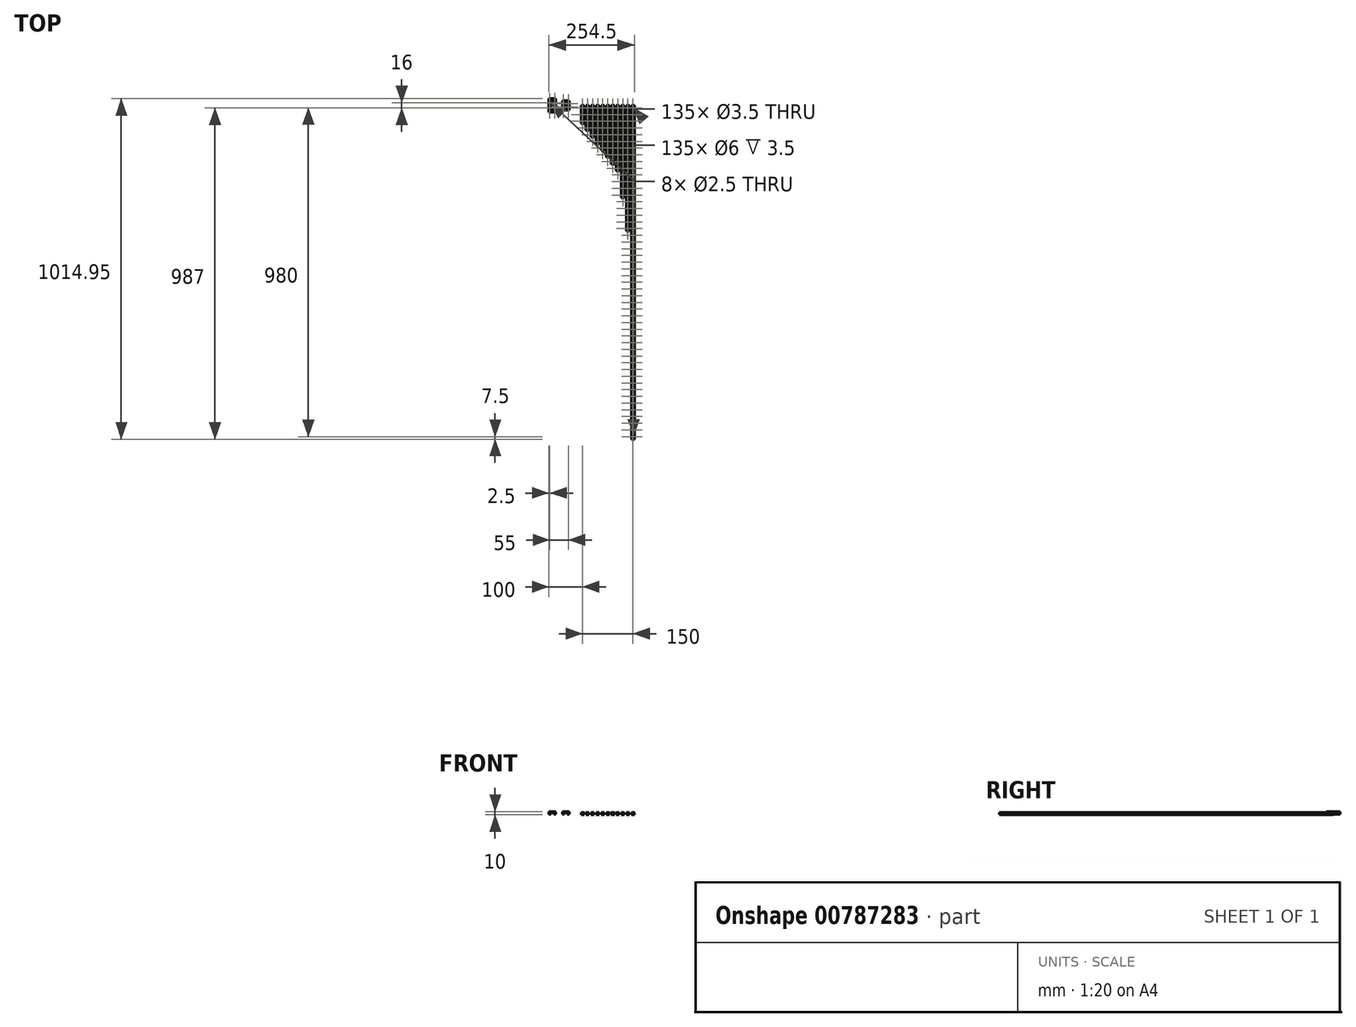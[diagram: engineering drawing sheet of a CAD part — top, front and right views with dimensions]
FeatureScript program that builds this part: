
annotation { "Feature Type Name" : "Feature", "Feature Type Description" : "" }
export const myFeature = defineFeature(function(context is Context, id is Id, definition is map)
    precondition{}
    {
        {
            var Q0;
            Q0=qCreatedBy(makeId("Front.planeOp"),FACE);
            var sketch = newSketch(context, id + "F0", { "sketchPlane" : qUnion([Q0])});
            skPoint(sketch, "E0.middle", {"position": v(0, 0) * mm});
            skLineSegment(sketch, "E1.bottom", {"start": v(4.15, -3.25) * mm, "end": v(-4.15, -3.25) * mm});
            skLineSegment(sketch, "E1.top", {"start": v(4.15, 3.25) * mm, "end": v(-4.15, 3.25) * mm});
            skLineSegment(sketch, "E1.left", {"start": v(4.5, -2.9) * mm, "end": v(4.5, 0.28) * mm});
            skLineSegment(sketch, "E1.right", {"start": v(-4.5, -2.9) * mm, "end": v(-4.5, 0.28) * mm});
            skArc(sketch, "E2", {"start": v(-4.5, 0.28) * mm, "mid": v(-4.1, 0.49) * mm, "end": v(-3.83, 0.85) * mm});
            skArc(sketch, "E3", {"start": v(4.5, 2.22) * mm, "mid": v(4.1, 2.01) * mm, "end": v(3.83, 1.65) * mm});
            skLineSegment(sketch, "E4", {"start": v(3.3, 1.65) * mm, "end": v(3.83, 1.65) * mm});
            skLineSegment(sketch, "E5", {"start": v(3.3, 0.85) * mm, "end": v(3.83, 0.85) * mm});
            skLineSegment(sketch, "E6", {"start": v(-3.3, 0.85) * mm, "end": v(-3.83, 0.85) * mm});
            skLineSegment(sketch, "E7", {"start": v(-3.3, 1.65) * mm, "end": v(-3.83, 1.65) * mm});
            skLineSegment(sketch, "E8", {"start": v(-4.5, 2.9) * mm, "end": v(-4.15, 3.25) * mm});
            skLineSegment(sketch, "E9.MirrorCS", {"start": v(4.5, 2.9) * mm, "end": v(4.15, 3.25) * mm});
            skLineSegment(sketch, "E10.MirrorCS", {"start": v(4.5, -2.9) * mm, "end": v(4.15, -3.25) * mm});
            skLineSegment(sketch, "E11.MirrorCS", {"start": v(-4.5, -2.9) * mm, "end": v(-4.15, -3.25) * mm});
            skPoint(sketch, "E12.orphan", {"position": v(-4.5, 3.25) * mm});
            skLineSegment(sketch, "E13.trimOffspring", {"start": v(-4.5, 2.22) * mm, "end": v(-4.5, 2.9) * mm});
            skArc(sketch, "E14.trimOffspring", {"start": v(-3.83, 1.65) * mm, "mid": v(-4.1, 2.01) * mm, "end": v(-4.5, 2.22) * mm});
            skPoint(sketch, "E15.orphan", {"position": v(4.5, 3.25) * mm});
            skLineSegment(sketch, "E16.trimOffspring", {"start": v(4.5, 2.22) * mm, "end": v(4.5, 2.9) * mm});
            skArc(sketch, "E17.trimOffspring", {"start": v(3.83, 0.85) * mm, "mid": v(4.1, 0.49) * mm, "end": v(4.5, 0.28) * mm});
            skPoint(sketch, "E18.orphan", {"position": v(4.5, -3.25) * mm});
            skPoint(sketch, "E19.orphan", {"position": v(-4.5, -3.25) * mm});
            skLineSegment(sketch, "E20", {"start": v(-3.3, 1.65) * mm, "end": v(-3.3, 0.85) * mm});
            skLineSegment(sketch, "E21", {"start": v(3.3, 1.65) * mm, "end": v(3.3, 0.85) * mm});
            skLineSegment(sketch, "E22", {"start": v(-4.75, 1.25) * mm, "end": v(4.75, 1.25) * mm, "construction": true});
            skLineSegment(sketch, "E23.1.0.0", {"start": v(10.25, 1.25) * mm, "end": v(19.75, 1.25) * mm, "construction": true});
            skLineSegment(sketch, "E23.1.0.1", {"start": v(10.5, -2.9) * mm, "end": v(10.5, 0.28) * mm});
            skLineSegment(sketch, "E23.1.0.2", {"start": v(19.5, -2.9) * mm, "end": v(19.5, 0.28) * mm});
            skLineSegment(sketch, "E23.1.0.3", {"start": v(19.15, -3.25) * mm, "end": v(10.85, -3.25) * mm});
            skLineSegment(sketch, "E23.1.0.4", {"start": v(19.15, 3.25) * mm, "end": v(10.85, 3.25) * mm});
            skPoint(sketch, "E23.1.0.5", {"position": v(15, 0) * mm});
            skPoint(sketch, "E23.1.0.6", {"position": v(10.5, -3.25) * mm});
            skPoint(sketch, "E23.1.0.7", {"position": v(10.5, 3.25) * mm});
            skPoint(sketch, "E23.1.0.8", {"position": v(19.5, 3.25) * mm});
            skPoint(sketch, "E23.1.0.9", {"position": v(19.5, -3.25) * mm});
            skPoint(sketch, "E23.1.0.10", {"position": v(15, 0) * mm});
            skLineSegment(sketch, "E23.1.0.11", {"start": v(19.5, -2.9) * mm, "end": v(19.15, -3.25) * mm});
            skLineSegment(sketch, "E23.1.0.12", {"start": v(19.5, 2.9) * mm, "end": v(19.15, 3.25) * mm});
            skLineSegment(sketch, "E23.1.0.13", {"start": v(10.5, -2.9) * mm, "end": v(10.85, -3.25) * mm});
            skLineSegment(sketch, "E23.1.0.14", {"start": v(11.7, 1.65) * mm, "end": v(11.17, 1.65) * mm});
            skLineSegment(sketch, "E23.1.0.15", {"start": v(10.5, 2.22) * mm, "end": v(10.5, 2.9) * mm});
            skLineSegment(sketch, "E23.1.0.16", {"start": v(19.5, 2.22) * mm, "end": v(19.5, 2.9) * mm});
            skArc(sketch, "E23.1.0.17", {"start": v(18.83, 0.85) * mm, "mid": v(19.1, 0.49) * mm, "end": v(19.5, 0.28) * mm});
            skLineSegment(sketch, "E23.1.0.18", {"start": v(11.7, 1.65) * mm, "end": v(11.7, 0.85) * mm});
            skLineSegment(sketch, "E23.1.0.19", {"start": v(18.3, 0.85) * mm, "end": v(18.83, 0.85) * mm});
            skLineSegment(sketch, "E23.1.0.20", {"start": v(11.7, 0.85) * mm, "end": v(11.17, 0.85) * mm});
            skArc(sketch, "E23.1.0.21", {"start": v(10.5, 0.28) * mm, "mid": v(10.9, 0.49) * mm, "end": v(11.17, 0.85) * mm});
            skLineSegment(sketch, "E23.1.0.22", {"start": v(10.5, 2.9) * mm, "end": v(10.85, 3.25) * mm});
            skArc(sketch, "E23.1.0.23", {"start": v(11.17, 1.65) * mm, "mid": v(10.9, 2.01) * mm, "end": v(10.5, 2.22) * mm});
            skLineSegment(sketch, "E23.1.0.24", {"start": v(18.3, 1.65) * mm, "end": v(18.83, 1.65) * mm});
            skArc(sketch, "E23.1.0.25", {"start": v(19.5, 2.22) * mm, "mid": v(19.1, 2.01) * mm, "end": v(18.83, 1.65) * mm});
            skArc(sketch, "E23.1.0.26", {"start": v(18.83, 0.85) * mm, "mid": v(19.1, 0.49) * mm, "end": v(19.5, 0.28) * mm});
            skLineSegment(sketch, "E23.1.0.27", {"start": v(18.3, 1.65) * mm, "end": v(18.3, 0.85) * mm});
            skLineSegment(sketch, "E23.2.0.0", {"start": v(25.25, 1.25) * mm, "end": v(34.75, 1.25) * mm, "construction": true});
            skLineSegment(sketch, "E23.2.0.1", {"start": v(25.5, -2.9) * mm, "end": v(25.5, 0.28) * mm});
            skLineSegment(sketch, "E23.2.0.2", {"start": v(34.5, -2.9) * mm, "end": v(34.5, 0.28) * mm});
            skLineSegment(sketch, "E23.2.0.3", {"start": v(34.15, -3.25) * mm, "end": v(25.85, -3.25) * mm});
            skLineSegment(sketch, "E23.2.0.4", {"start": v(34.15, 3.25) * mm, "end": v(25.85, 3.25) * mm});
            skPoint(sketch, "E23.2.0.5", {"position": v(30, 0) * mm});
            skPoint(sketch, "E23.2.0.6", {"position": v(25.5, -3.25) * mm});
            skPoint(sketch, "E23.2.0.7", {"position": v(25.5, 3.25) * mm});
            skPoint(sketch, "E23.2.0.8", {"position": v(34.5, 3.25) * mm});
            skPoint(sketch, "E23.2.0.9", {"position": v(34.5, -3.25) * mm});
            skPoint(sketch, "E23.2.0.10", {"position": v(30, 0) * mm});
            skLineSegment(sketch, "E23.2.0.11", {"start": v(34.5, -2.9) * mm, "end": v(34.15, -3.25) * mm});
            skLineSegment(sketch, "E23.2.0.12", {"start": v(34.5, 2.9) * mm, "end": v(34.15, 3.25) * mm});
            skLineSegment(sketch, "E23.2.0.13", {"start": v(25.5, -2.9) * mm, "end": v(25.85, -3.25) * mm});
            skLineSegment(sketch, "E23.2.0.14", {"start": v(26.7, 1.65) * mm, "end": v(26.17, 1.65) * mm});
            skLineSegment(sketch, "E23.2.0.15", {"start": v(25.5, 2.22) * mm, "end": v(25.5, 2.9) * mm});
            skLineSegment(sketch, "E23.2.0.16", {"start": v(34.5, 2.22) * mm, "end": v(34.5, 2.9) * mm});
            skArc(sketch, "E23.2.0.17", {"start": v(33.83, 0.85) * mm, "mid": v(34.1, 0.49) * mm, "end": v(34.5, 0.28) * mm});
            skLineSegment(sketch, "E23.2.0.18", {"start": v(26.7, 1.65) * mm, "end": v(26.7, 0.85) * mm});
            skLineSegment(sketch, "E23.2.0.19", {"start": v(33.3, 0.85) * mm, "end": v(33.83, 0.85) * mm});
            skLineSegment(sketch, "E23.2.0.20", {"start": v(26.7, 0.85) * mm, "end": v(26.17, 0.85) * mm});
            skArc(sketch, "E23.2.0.21", {"start": v(25.5, 0.28) * mm, "mid": v(25.9, 0.49) * mm, "end": v(26.17, 0.85) * mm});
            skLineSegment(sketch, "E23.2.0.22", {"start": v(25.5, 2.9) * mm, "end": v(25.85, 3.25) * mm});
            skArc(sketch, "E23.2.0.23", {"start": v(26.17, 1.65) * mm, "mid": v(25.9, 2.01) * mm, "end": v(25.5, 2.22) * mm});
            skLineSegment(sketch, "E23.2.0.24", {"start": v(33.3, 1.65) * mm, "end": v(33.83, 1.65) * mm});
            skArc(sketch, "E23.2.0.25", {"start": v(34.5, 2.22) * mm, "mid": v(34.1, 2.01) * mm, "end": v(33.83, 1.65) * mm});
            skArc(sketch, "E23.2.0.26", {"start": v(33.83, 0.85) * mm, "mid": v(34.1, 0.49) * mm, "end": v(34.5, 0.28) * mm});
            skLineSegment(sketch, "E23.2.0.27", {"start": v(33.3, 1.65) * mm, "end": v(33.3, 0.85) * mm});
            skLineSegment(sketch, "E23.3.0.0", {"start": v(40.25, 1.25) * mm, "end": v(49.75, 1.25) * mm, "construction": true});
            skLineSegment(sketch, "E23.3.0.1", {"start": v(40.5, -2.9) * mm, "end": v(40.5, 0.28) * mm});
            skLineSegment(sketch, "E23.3.0.2", {"start": v(49.5, -2.9) * mm, "end": v(49.5, 0.28) * mm});
            skLineSegment(sketch, "E23.3.0.3", {"start": v(49.15, -3.25) * mm, "end": v(40.85, -3.25) * mm});
            skLineSegment(sketch, "E23.3.0.4", {"start": v(49.15, 3.25) * mm, "end": v(40.85, 3.25) * mm});
            skPoint(sketch, "E23.3.0.5", {"position": v(45, 0) * mm});
            skPoint(sketch, "E23.3.0.6", {"position": v(40.5, -3.25) * mm});
            skPoint(sketch, "E23.3.0.7", {"position": v(40.5, 3.25) * mm});
            skPoint(sketch, "E23.3.0.8", {"position": v(49.5, 3.25) * mm});
            skPoint(sketch, "E23.3.0.9", {"position": v(49.5, -3.25) * mm});
            skPoint(sketch, "E23.3.0.10", {"position": v(45, 0) * mm});
            skLineSegment(sketch, "E23.3.0.11", {"start": v(49.5, -2.9) * mm, "end": v(49.15, -3.25) * mm});
            skLineSegment(sketch, "E23.3.0.12", {"start": v(49.5, 2.9) * mm, "end": v(49.15, 3.25) * mm});
            skLineSegment(sketch, "E23.3.0.13", {"start": v(40.5, -2.9) * mm, "end": v(40.85, -3.25) * mm});
            skLineSegment(sketch, "E23.3.0.14", {"start": v(41.7, 1.65) * mm, "end": v(41.17, 1.65) * mm});
            skLineSegment(sketch, "E23.3.0.15", {"start": v(40.5, 2.22) * mm, "end": v(40.5, 2.9) * mm});
            skLineSegment(sketch, "E23.3.0.16", {"start": v(49.5, 2.22) * mm, "end": v(49.5, 2.9) * mm});
            skArc(sketch, "E23.3.0.17", {"start": v(48.83, 0.85) * mm, "mid": v(49.1, 0.49) * mm, "end": v(49.5, 0.28) * mm});
            skLineSegment(sketch, "E23.3.0.18", {"start": v(41.7, 1.65) * mm, "end": v(41.7, 0.85) * mm});
            skLineSegment(sketch, "E23.3.0.19", {"start": v(48.3, 0.85) * mm, "end": v(48.83, 0.85) * mm});
            skLineSegment(sketch, "E23.3.0.20", {"start": v(41.7, 0.85) * mm, "end": v(41.17, 0.85) * mm});
            skArc(sketch, "E23.3.0.21", {"start": v(40.5, 0.28) * mm, "mid": v(40.9, 0.49) * mm, "end": v(41.17, 0.85) * mm});
            skLineSegment(sketch, "E23.3.0.22", {"start": v(40.5, 2.9) * mm, "end": v(40.85, 3.25) * mm});
            skArc(sketch, "E23.3.0.23", {"start": v(41.17, 1.65) * mm, "mid": v(40.9, 2.01) * mm, "end": v(40.5, 2.22) * mm});
            skLineSegment(sketch, "E23.3.0.24", {"start": v(48.3, 1.65) * mm, "end": v(48.83, 1.65) * mm});
            skArc(sketch, "E23.3.0.25", {"start": v(49.5, 2.22) * mm, "mid": v(49.1, 2.01) * mm, "end": v(48.83, 1.65) * mm});
            skArc(sketch, "E23.3.0.26", {"start": v(48.83, 0.85) * mm, "mid": v(49.1, 0.49) * mm, "end": v(49.5, 0.28) * mm});
            skLineSegment(sketch, "E23.3.0.27", {"start": v(48.3, 1.65) * mm, "end": v(48.3, 0.85) * mm});
            skLineSegment(sketch, "E23.4.0.0", {"start": v(55.25, 1.25) * mm, "end": v(64.75, 1.25) * mm, "construction": true});
            skLineSegment(sketch, "E23.4.0.1", {"start": v(55.5, -2.9) * mm, "end": v(55.5, 0.28) * mm});
            skLineSegment(sketch, "E23.4.0.2", {"start": v(64.5, -2.9) * mm, "end": v(64.5, 0.28) * mm});
            skLineSegment(sketch, "E23.4.0.3", {"start": v(64.15, -3.25) * mm, "end": v(55.85, -3.25) * mm});
            skLineSegment(sketch, "E23.4.0.4", {"start": v(64.15, 3.25) * mm, "end": v(55.85, 3.25) * mm});
            skPoint(sketch, "E23.4.0.5", {"position": v(60, 0) * mm});
            skPoint(sketch, "E23.4.0.6", {"position": v(55.5, -3.25) * mm});
            skPoint(sketch, "E23.4.0.7", {"position": v(55.5, 3.25) * mm});
            skPoint(sketch, "E23.4.0.8", {"position": v(64.5, 3.25) * mm});
            skPoint(sketch, "E23.4.0.9", {"position": v(64.5, -3.25) * mm});
            skPoint(sketch, "E23.4.0.10", {"position": v(60, 0) * mm});
            skLineSegment(sketch, "E23.4.0.11", {"start": v(64.5, -2.9) * mm, "end": v(64.15, -3.25) * mm});
            skLineSegment(sketch, "E23.4.0.12", {"start": v(64.5, 2.9) * mm, "end": v(64.15, 3.25) * mm});
            skLineSegment(sketch, "E23.4.0.13", {"start": v(55.5, -2.9) * mm, "end": v(55.85, -3.25) * mm});
            skLineSegment(sketch, "E23.4.0.14", {"start": v(56.7, 1.65) * mm, "end": v(56.17, 1.65) * mm});
            skLineSegment(sketch, "E23.4.0.15", {"start": v(55.5, 2.22) * mm, "end": v(55.5, 2.9) * mm});
            skLineSegment(sketch, "E23.4.0.16", {"start": v(64.5, 2.22) * mm, "end": v(64.5, 2.9) * mm});
            skArc(sketch, "E23.4.0.17", {"start": v(63.83, 0.85) * mm, "mid": v(64.1, 0.49) * mm, "end": v(64.5, 0.28) * mm});
            skLineSegment(sketch, "E23.4.0.18", {"start": v(56.7, 1.65) * mm, "end": v(56.7, 0.85) * mm});
            skLineSegment(sketch, "E23.4.0.19", {"start": v(63.3, 0.85) * mm, "end": v(63.83, 0.85) * mm});
            skLineSegment(sketch, "E23.4.0.20", {"start": v(56.7, 0.85) * mm, "end": v(56.17, 0.85) * mm});
            skArc(sketch, "E23.4.0.21", {"start": v(55.5, 0.28) * mm, "mid": v(55.9, 0.49) * mm, "end": v(56.17, 0.85) * mm});
            skLineSegment(sketch, "E23.4.0.22", {"start": v(55.5, 2.9) * mm, "end": v(55.85, 3.25) * mm});
            skArc(sketch, "E23.4.0.23", {"start": v(56.17, 1.65) * mm, "mid": v(55.9, 2.01) * mm, "end": v(55.5, 2.22) * mm});
            skLineSegment(sketch, "E23.4.0.24", {"start": v(63.3, 1.65) * mm, "end": v(63.83, 1.65) * mm});
            skArc(sketch, "E23.4.0.25", {"start": v(64.5, 2.22) * mm, "mid": v(64.1, 2.01) * mm, "end": v(63.83, 1.65) * mm});
            skArc(sketch, "E23.4.0.26", {"start": v(63.83, 0.85) * mm, "mid": v(64.1, 0.49) * mm, "end": v(64.5, 0.28) * mm});
            skLineSegment(sketch, "E23.4.0.27", {"start": v(63.3, 1.65) * mm, "end": v(63.3, 0.85) * mm});
            skLineSegment(sketch, "E23.5.0.0", {"start": v(70.25, 1.25) * mm, "end": v(79.75, 1.25) * mm, "construction": true});
            skLineSegment(sketch, "E23.5.0.1", {"start": v(70.5, -2.9) * mm, "end": v(70.5, 0.28) * mm});
            skLineSegment(sketch, "E23.5.0.2", {"start": v(79.5, -2.9) * mm, "end": v(79.5, 0.28) * mm});
            skLineSegment(sketch, "E23.5.0.3", {"start": v(79.15, -3.25) * mm, "end": v(70.85, -3.25) * mm});
            skLineSegment(sketch, "E23.5.0.4", {"start": v(79.15, 3.25) * mm, "end": v(70.85, 3.25) * mm});
            skPoint(sketch, "E23.5.0.5", {"position": v(75, 0) * mm});
            skPoint(sketch, "E23.5.0.6", {"position": v(70.5, -3.25) * mm});
            skPoint(sketch, "E23.5.0.7", {"position": v(70.5, 3.25) * mm});
            skPoint(sketch, "E23.5.0.8", {"position": v(79.5, 3.25) * mm});
            skPoint(sketch, "E23.5.0.9", {"position": v(79.5, -3.25) * mm});
            skPoint(sketch, "E23.5.0.10", {"position": v(75, 0) * mm});
            skLineSegment(sketch, "E23.5.0.11", {"start": v(79.5, -2.9) * mm, "end": v(79.15, -3.25) * mm});
            skLineSegment(sketch, "E23.5.0.12", {"start": v(79.5, 2.9) * mm, "end": v(79.15, 3.25) * mm});
            skLineSegment(sketch, "E23.5.0.13", {"start": v(70.5, -2.9) * mm, "end": v(70.85, -3.25) * mm});
            skLineSegment(sketch, "E23.5.0.14", {"start": v(71.7, 1.65) * mm, "end": v(71.17, 1.65) * mm});
            skLineSegment(sketch, "E23.5.0.15", {"start": v(70.5, 2.22) * mm, "end": v(70.5, 2.9) * mm});
            skLineSegment(sketch, "E23.5.0.16", {"start": v(79.5, 2.22) * mm, "end": v(79.5, 2.9) * mm});
            skArc(sketch, "E23.5.0.17", {"start": v(78.83, 0.85) * mm, "mid": v(79.1, 0.49) * mm, "end": v(79.5, 0.28) * mm});
            skLineSegment(sketch, "E23.5.0.18", {"start": v(71.7, 1.65) * mm, "end": v(71.7, 0.85) * mm});
            skLineSegment(sketch, "E23.5.0.19", {"start": v(78.3, 0.85) * mm, "end": v(78.83, 0.85) * mm});
            skLineSegment(sketch, "E23.5.0.20", {"start": v(71.7, 0.85) * mm, "end": v(71.17, 0.85) * mm});
            skArc(sketch, "E23.5.0.21", {"start": v(70.5, 0.28) * mm, "mid": v(70.9, 0.49) * mm, "end": v(71.17, 0.85) * mm});
            skLineSegment(sketch, "E23.5.0.22", {"start": v(70.5, 2.9) * mm, "end": v(70.85, 3.25) * mm});
            skArc(sketch, "E23.5.0.23", {"start": v(71.17, 1.65) * mm, "mid": v(70.9, 2.01) * mm, "end": v(70.5, 2.22) * mm});
            skLineSegment(sketch, "E23.5.0.24", {"start": v(78.3, 1.65) * mm, "end": v(78.83, 1.65) * mm});
            skArc(sketch, "E23.5.0.25", {"start": v(79.5, 2.22) * mm, "mid": v(79.1, 2.01) * mm, "end": v(78.83, 1.65) * mm});
            skArc(sketch, "E23.5.0.26", {"start": v(78.83, 0.85) * mm, "mid": v(79.1, 0.49) * mm, "end": v(79.5, 0.28) * mm});
            skLineSegment(sketch, "E23.5.0.27", {"start": v(78.3, 1.65) * mm, "end": v(78.3, 0.85) * mm});
            skLineSegment(sketch, "E23.6.0.0", {"start": v(85.25, 1.25) * mm, "end": v(94.75, 1.25) * mm, "construction": true});
            skLineSegment(sketch, "E23.6.0.1", {"start": v(85.5, -2.9) * mm, "end": v(85.5, 0.28) * mm});
            skLineSegment(sketch, "E23.6.0.2", {"start": v(94.5, -2.9) * mm, "end": v(94.5, 0.28) * mm});
            skLineSegment(sketch, "E23.6.0.3", {"start": v(94.15, -3.25) * mm, "end": v(85.85, -3.25) * mm});
            skLineSegment(sketch, "E23.6.0.4", {"start": v(94.15, 3.25) * mm, "end": v(85.85, 3.25) * mm});
            skPoint(sketch, "E23.6.0.5", {"position": v(90, 0) * mm});
            skPoint(sketch, "E23.6.0.6", {"position": v(85.5, -3.25) * mm});
            skPoint(sketch, "E23.6.0.7", {"position": v(85.5, 3.25) * mm});
            skPoint(sketch, "E23.6.0.8", {"position": v(94.5, 3.25) * mm});
            skPoint(sketch, "E23.6.0.9", {"position": v(94.5, -3.25) * mm});
            skPoint(sketch, "E23.6.0.10", {"position": v(90, 0) * mm});
            skLineSegment(sketch, "E23.6.0.11", {"start": v(94.5, -2.9) * mm, "end": v(94.15, -3.25) * mm});
            skLineSegment(sketch, "E23.6.0.12", {"start": v(94.5, 2.9) * mm, "end": v(94.15, 3.25) * mm});
            skLineSegment(sketch, "E23.6.0.13", {"start": v(85.5, -2.9) * mm, "end": v(85.85, -3.25) * mm});
            skLineSegment(sketch, "E23.6.0.14", {"start": v(86.7, 1.65) * mm, "end": v(86.17, 1.65) * mm});
            skLineSegment(sketch, "E23.6.0.15", {"start": v(85.5, 2.22) * mm, "end": v(85.5, 2.9) * mm});
            skLineSegment(sketch, "E23.6.0.16", {"start": v(94.5, 2.22) * mm, "end": v(94.5, 2.9) * mm});
            skArc(sketch, "E23.6.0.17", {"start": v(93.83, 0.85) * mm, "mid": v(94.1, 0.49) * mm, "end": v(94.5, 0.28) * mm});
            skLineSegment(sketch, "E23.6.0.18", {"start": v(86.7, 1.65) * mm, "end": v(86.7, 0.85) * mm});
            skLineSegment(sketch, "E23.6.0.19", {"start": v(93.3, 0.85) * mm, "end": v(93.83, 0.85) * mm});
            skLineSegment(sketch, "E23.6.0.20", {"start": v(86.7, 0.85) * mm, "end": v(86.17, 0.85) * mm});
            skArc(sketch, "E23.6.0.21", {"start": v(85.5, 0.28) * mm, "mid": v(85.9, 0.49) * mm, "end": v(86.17, 0.85) * mm});
            skLineSegment(sketch, "E23.6.0.22", {"start": v(85.5, 2.9) * mm, "end": v(85.85, 3.25) * mm});
            skArc(sketch, "E23.6.0.23", {"start": v(86.17, 1.65) * mm, "mid": v(85.9, 2.01) * mm, "end": v(85.5, 2.22) * mm});
            skLineSegment(sketch, "E23.6.0.24", {"start": v(93.3, 1.65) * mm, "end": v(93.83, 1.65) * mm});
            skArc(sketch, "E23.6.0.25", {"start": v(94.5, 2.22) * mm, "mid": v(94.1, 2.01) * mm, "end": v(93.83, 1.65) * mm});
            skArc(sketch, "E23.6.0.26", {"start": v(93.83, 0.85) * mm, "mid": v(94.1, 0.49) * mm, "end": v(94.5, 0.28) * mm});
            skLineSegment(sketch, "E23.6.0.27", {"start": v(93.3, 1.65) * mm, "end": v(93.3, 0.85) * mm});
            skLineSegment(sketch, "E23.direction1", {"start": v(-4.5, -3.25) * mm, "end": v(10.5, -3.25) * mm, "construction": true});
            skLineSegment(sketch, "E24.0.7.0", {"start": v(100.25, 1.25) * mm, "end": v(109.75, 1.25) * mm, "construction": true});
            skLineSegment(sketch, "E24.3.7.0", {"start": v(100.5, -2.9) * mm, "end": v(100.5, 0.28) * mm});
            skLineSegment(sketch, "E24.6.7.0", {"start": v(109.5, -2.9) * mm, "end": v(109.5, 0.28) * mm});
            skLineSegment(sketch, "E24.9.7.0", {"start": v(109.15, -3.25) * mm, "end": v(100.85, -3.25) * mm});
            skLineSegment(sketch, "E24.12.7.0", {"start": v(109.15, 3.25) * mm, "end": v(100.85, 3.25) * mm});
            skPoint(sketch, "E24.15.7.0", {"position": v(105, 0) * mm});
            skPoint(sketch, "E24.16.7.0", {"position": v(100.5, -3.25) * mm});
            skPoint(sketch, "E24.17.7.0", {"position": v(100.5, 3.25) * mm});
            skPoint(sketch, "E24.18.7.0", {"position": v(109.5, 3.25) * mm});
            skPoint(sketch, "E24.19.7.0", {"position": v(109.5, -3.25) * mm});
            skPoint(sketch, "E24.20.7.0", {"position": v(105, 0) * mm});
            skLineSegment(sketch, "E24.21.7.0", {"start": v(109.5, -2.9) * mm, "end": v(109.15, -3.25) * mm});
            skLineSegment(sketch, "E24.24.7.0", {"start": v(109.5, 2.9) * mm, "end": v(109.15, 3.25) * mm});
            skLineSegment(sketch, "E24.27.7.0", {"start": v(100.5, -2.9) * mm, "end": v(100.85, -3.25) * mm});
            skLineSegment(sketch, "E24.30.7.0", {"start": v(101.7, 1.65) * mm, "end": v(101.17, 1.65) * mm});
            skLineSegment(sketch, "E24.33.7.0", {"start": v(100.5, 2.22) * mm, "end": v(100.5, 2.9) * mm});
            skLineSegment(sketch, "E24.36.7.0", {"start": v(109.5, 2.22) * mm, "end": v(109.5, 2.9) * mm});
            skArc(sketch, "E24.39.7.0", {"start": v(108.83, 0.85) * mm, "mid": v(109.1, 0.49) * mm, "end": v(109.5, 0.28) * mm});
            skLineSegment(sketch, "E24.43.7.0", {"start": v(101.7, 1.65) * mm, "end": v(101.7, 0.85) * mm});
            skLineSegment(sketch, "E24.46.7.0", {"start": v(108.3, 0.85) * mm, "end": v(108.83, 0.85) * mm});
            skLineSegment(sketch, "E24.49.7.0", {"start": v(101.7, 0.85) * mm, "end": v(101.17, 0.85) * mm});
            skArc(sketch, "E24.52.7.0", {"start": v(100.5, 0.28) * mm, "mid": v(100.9, 0.49) * mm, "end": v(101.17, 0.85) * mm});
            skLineSegment(sketch, "E24.56.7.0", {"start": v(100.5, 2.9) * mm, "end": v(100.85, 3.25) * mm});
            skArc(sketch, "E24.59.7.0", {"start": v(101.17, 1.65) * mm, "mid": v(100.9, 2.01) * mm, "end": v(100.5, 2.22) * mm});
            skLineSegment(sketch, "E24.63.7.0", {"start": v(108.3, 1.65) * mm, "end": v(108.83, 1.65) * mm});
            skArc(sketch, "E24.66.7.0", {"start": v(109.5, 2.22) * mm, "mid": v(109.1, 2.01) * mm, "end": v(108.83, 1.65) * mm});
            skArc(sketch, "E24.70.7.0", {"start": v(108.83, 0.85) * mm, "mid": v(109.1, 0.49) * mm, "end": v(109.5, 0.28) * mm});
            skLineSegment(sketch, "E24.74.7.0", {"start": v(108.3, 1.65) * mm, "end": v(108.3, 0.85) * mm});
            skLineSegment(sketch, "E24.0.8.0", {"start": v(115.25, 1.25) * mm, "end": v(124.75, 1.25) * mm, "construction": true});
            skLineSegment(sketch, "E24.3.8.0", {"start": v(115.5, -2.9) * mm, "end": v(115.5, 0.28) * mm});
            skLineSegment(sketch, "E24.6.8.0", {"start": v(124.5, -2.9) * mm, "end": v(124.5, 0.28) * mm});
            skLineSegment(sketch, "E24.9.8.0", {"start": v(124.15, -3.25) * mm, "end": v(115.85, -3.25) * mm});
            skLineSegment(sketch, "E24.12.8.0", {"start": v(124.15, 3.25) * mm, "end": v(115.85, 3.25) * mm});
            skPoint(sketch, "E24.15.8.0", {"position": v(120, 0) * mm});
            skPoint(sketch, "E24.16.8.0", {"position": v(115.5, -3.25) * mm});
            skPoint(sketch, "E24.17.8.0", {"position": v(115.5, 3.25) * mm});
            skPoint(sketch, "E24.18.8.0", {"position": v(124.5, 3.25) * mm});
            skPoint(sketch, "E24.19.8.0", {"position": v(124.5, -3.25) * mm});
            skPoint(sketch, "E24.20.8.0", {"position": v(120, 0) * mm});
            skLineSegment(sketch, "E24.21.8.0", {"start": v(124.5, -2.9) * mm, "end": v(124.15, -3.25) * mm});
            skLineSegment(sketch, "E24.24.8.0", {"start": v(124.5, 2.9) * mm, "end": v(124.15, 3.25) * mm});
            skLineSegment(sketch, "E24.27.8.0", {"start": v(115.5, -2.9) * mm, "end": v(115.85, -3.25) * mm});
            skLineSegment(sketch, "E24.30.8.0", {"start": v(116.7, 1.65) * mm, "end": v(116.17, 1.65) * mm});
            skLineSegment(sketch, "E24.33.8.0", {"start": v(115.5, 2.22) * mm, "end": v(115.5, 2.9) * mm});
            skLineSegment(sketch, "E24.36.8.0", {"start": v(124.5, 2.22) * mm, "end": v(124.5, 2.9) * mm});
            skArc(sketch, "E24.39.8.0", {"start": v(123.83, 0.85) * mm, "mid": v(124.1, 0.49) * mm, "end": v(124.5, 0.28) * mm});
            skLineSegment(sketch, "E24.43.8.0", {"start": v(116.7, 1.65) * mm, "end": v(116.7, 0.85) * mm});
            skLineSegment(sketch, "E24.46.8.0", {"start": v(123.3, 0.85) * mm, "end": v(123.83, 0.85) * mm});
            skLineSegment(sketch, "E24.49.8.0", {"start": v(116.7, 0.85) * mm, "end": v(116.17, 0.85) * mm});
            skArc(sketch, "E24.52.8.0", {"start": v(115.5, 0.28) * mm, "mid": v(115.9, 0.49) * mm, "end": v(116.17, 0.85) * mm});
            skLineSegment(sketch, "E24.56.8.0", {"start": v(115.5, 2.9) * mm, "end": v(115.85, 3.25) * mm});
            skArc(sketch, "E24.59.8.0", {"start": v(116.17, 1.65) * mm, "mid": v(115.9, 2.01) * mm, "end": v(115.5, 2.22) * mm});
            skLineSegment(sketch, "E24.63.8.0", {"start": v(123.3, 1.65) * mm, "end": v(123.83, 1.65) * mm});
            skArc(sketch, "E24.66.8.0", {"start": v(124.5, 2.22) * mm, "mid": v(124.1, 2.01) * mm, "end": v(123.83, 1.65) * mm});
            skArc(sketch, "E24.70.8.0", {"start": v(123.83, 0.85) * mm, "mid": v(124.1, 0.49) * mm, "end": v(124.5, 0.28) * mm});
            skLineSegment(sketch, "E24.74.8.0", {"start": v(123.3, 1.65) * mm, "end": v(123.3, 0.85) * mm});
            skLineSegment(sketch, "E24.0.9.0", {"start": v(130.25, 1.25) * mm, "end": v(139.75, 1.25) * mm, "construction": true});
            skLineSegment(sketch, "E24.3.9.0", {"start": v(130.5, -2.9) * mm, "end": v(130.5, 0.28) * mm});
            skLineSegment(sketch, "E24.6.9.0", {"start": v(139.5, -2.9) * mm, "end": v(139.5, 0.28) * mm});
            skLineSegment(sketch, "E24.9.9.0", {"start": v(139.15, -3.25) * mm, "end": v(130.85, -3.25) * mm});
            skLineSegment(sketch, "E24.12.9.0", {"start": v(139.15, 3.25) * mm, "end": v(130.85, 3.25) * mm});
            skPoint(sketch, "E24.15.9.0", {"position": v(135, 0) * mm});
            skPoint(sketch, "E24.16.9.0", {"position": v(130.5, -3.25) * mm});
            skPoint(sketch, "E24.17.9.0", {"position": v(130.5, 3.25) * mm});
            skPoint(sketch, "E24.18.9.0", {"position": v(139.5, 3.25) * mm});
            skPoint(sketch, "E24.19.9.0", {"position": v(139.5, -3.25) * mm});
            skPoint(sketch, "E24.20.9.0", {"position": v(135, 0) * mm});
            skLineSegment(sketch, "E24.21.9.0", {"start": v(139.5, -2.9) * mm, "end": v(139.15, -3.25) * mm});
            skLineSegment(sketch, "E24.24.9.0", {"start": v(139.5, 2.9) * mm, "end": v(139.15, 3.25) * mm});
            skLineSegment(sketch, "E24.27.9.0", {"start": v(130.5, -2.9) * mm, "end": v(130.85, -3.25) * mm});
            skLineSegment(sketch, "E24.30.9.0", {"start": v(131.7, 1.65) * mm, "end": v(131.17, 1.65) * mm});
            skLineSegment(sketch, "E24.33.9.0", {"start": v(130.5, 2.22) * mm, "end": v(130.5, 2.9) * mm});
            skLineSegment(sketch, "E24.36.9.0", {"start": v(139.5, 2.22) * mm, "end": v(139.5, 2.9) * mm});
            skArc(sketch, "E24.39.9.0", {"start": v(138.83, 0.85) * mm, "mid": v(139.1, 0.49) * mm, "end": v(139.5, 0.28) * mm});
            skLineSegment(sketch, "E24.43.9.0", {"start": v(131.7, 1.65) * mm, "end": v(131.7, 0.85) * mm});
            skLineSegment(sketch, "E24.46.9.0", {"start": v(138.3, 0.85) * mm, "end": v(138.83, 0.85) * mm});
            skLineSegment(sketch, "E24.49.9.0", {"start": v(131.7, 0.85) * mm, "end": v(131.17, 0.85) * mm});
            skArc(sketch, "E24.52.9.0", {"start": v(130.5, 0.28) * mm, "mid": v(130.9, 0.49) * mm, "end": v(131.17, 0.85) * mm});
            skLineSegment(sketch, "E24.56.9.0", {"start": v(130.5, 2.9) * mm, "end": v(130.85, 3.25) * mm});
            skArc(sketch, "E24.59.9.0", {"start": v(131.17, 1.65) * mm, "mid": v(130.9, 2.01) * mm, "end": v(130.5, 2.22) * mm});
            skLineSegment(sketch, "E24.63.9.0", {"start": v(138.3, 1.65) * mm, "end": v(138.83, 1.65) * mm});
            skArc(sketch, "E24.66.9.0", {"start": v(139.5, 2.22) * mm, "mid": v(139.1, 2.01) * mm, "end": v(138.83, 1.65) * mm});
            skArc(sketch, "E24.70.9.0", {"start": v(138.83, 0.85) * mm, "mid": v(139.1, 0.49) * mm, "end": v(139.5, 0.28) * mm});
            skLineSegment(sketch, "E24.74.9.0", {"start": v(138.3, 1.65) * mm, "end": v(138.3, 0.85) * mm});
            skLineSegment(sketch, "E24.0.10.0", {"start": v(145.25, 1.25) * mm, "end": v(154.75, 1.25) * mm, "construction": true});
            skLineSegment(sketch, "E24.3.10.0", {"start": v(145.5, -2.9) * mm, "end": v(145.5, 0.28) * mm});
            skLineSegment(sketch, "E24.6.10.0", {"start": v(154.5, -2.9) * mm, "end": v(154.5, 0.28) * mm});
            skLineSegment(sketch, "E24.9.10.0", {"start": v(154.15, -3.25) * mm, "end": v(145.85, -3.25) * mm});
            skLineSegment(sketch, "E24.12.10.0", {"start": v(154.15, 3.25) * mm, "end": v(145.85, 3.25) * mm});
            skPoint(sketch, "E24.15.10.0", {"position": v(150, 0) * mm});
            skPoint(sketch, "E24.16.10.0", {"position": v(145.5, -3.25) * mm});
            skPoint(sketch, "E24.17.10.0", {"position": v(145.5, 3.25) * mm});
            skPoint(sketch, "E24.18.10.0", {"position": v(154.5, 3.25) * mm});
            skPoint(sketch, "E24.19.10.0", {"position": v(154.5, -3.25) * mm});
            skPoint(sketch, "E24.20.10.0", {"position": v(150, 0) * mm});
            skLineSegment(sketch, "E24.21.10.0", {"start": v(154.5, -2.9) * mm, "end": v(154.15, -3.25) * mm});
            skLineSegment(sketch, "E24.24.10.0", {"start": v(154.5, 2.9) * mm, "end": v(154.15, 3.25) * mm});
            skLineSegment(sketch, "E24.27.10.0", {"start": v(145.5, -2.9) * mm, "end": v(145.85, -3.25) * mm});
            skLineSegment(sketch, "E24.30.10.0", {"start": v(146.7, 1.65) * mm, "end": v(146.17, 1.65) * mm});
            skLineSegment(sketch, "E24.33.10.0", {"start": v(145.5, 2.22) * mm, "end": v(145.5, 2.9) * mm});
            skLineSegment(sketch, "E24.36.10.0", {"start": v(154.5, 2.22) * mm, "end": v(154.5, 2.9) * mm});
            skArc(sketch, "E24.39.10.0", {"start": v(153.83, 0.85) * mm, "mid": v(154.1, 0.49) * mm, "end": v(154.5, 0.28) * mm});
            skLineSegment(sketch, "E24.43.10.0", {"start": v(146.7, 1.65) * mm, "end": v(146.7, 0.85) * mm});
            skLineSegment(sketch, "E24.46.10.0", {"start": v(153.3, 0.85) * mm, "end": v(153.83, 0.85) * mm});
            skLineSegment(sketch, "E24.49.10.0", {"start": v(146.7, 0.85) * mm, "end": v(146.17, 0.85) * mm});
            skArc(sketch, "E24.52.10.0", {"start": v(145.5, 0.28) * mm, "mid": v(145.9, 0.49) * mm, "end": v(146.17, 0.85) * mm});
            skLineSegment(sketch, "E24.56.10.0", {"start": v(145.5, 2.9) * mm, "end": v(145.85, 3.25) * mm});
            skArc(sketch, "E24.59.10.0", {"start": v(146.17, 1.65) * mm, "mid": v(145.9, 2.01) * mm, "end": v(145.5, 2.22) * mm});
            skLineSegment(sketch, "E24.63.10.0", {"start": v(153.3, 1.65) * mm, "end": v(153.83, 1.65) * mm});
            skArc(sketch, "E24.66.10.0", {"start": v(154.5, 2.22) * mm, "mid": v(154.1, 2.01) * mm, "end": v(153.83, 1.65) * mm});
            skArc(sketch, "E24.70.10.0", {"start": v(153.83, 0.85) * mm, "mid": v(154.1, 0.49) * mm, "end": v(154.5, 0.28) * mm});
            skLineSegment(sketch, "E24.74.10.0", {"start": v(153.3, 1.65) * mm, "end": v(153.3, 0.85) * mm});
            skSolve(sketch);
        }
        {
            var Q0;
            Q0=makeQuery(id+"F0.imprint","IMPRINT",FACE,{"disambiguationData":[TD([[makeQuery(id+"F0.imprint","IMPRINT",EDGE,{"derivedFrom":sQuery(id+"F0.wireOp",EDGE,"E1.bottom")}),-1.0]])]});
            extrude(context, id + "F1", {"entities" : qUnion([Q0]), "depth" : 55 * mm, "offsetDistance" : 25 * mm});
        }
        {
            var Q0;
            Q0=makeQuery(id+"F0.imprint","IMPRINT",FACE,{"disambiguationData":[TD([[makeQuery(id+"F0.imprint","IMPRINT",EDGE,{"derivedFrom":sQuery(id+"F0.wireOp",EDGE,"E23.1.0.1")}),-1.0]])]});
            extrude(context, id + "F2", {"entities" : qUnion([Q0]), "depth" : 75 * mm, "offsetDistance" : 25 * mm});
        }
        {
            var Q0;
            Q0=makeQuery(id+"F0.imprint","IMPRINT",FACE,{"disambiguationData":[TD([[makeQuery(id+"F0.imprint","IMPRINT",EDGE,{"derivedFrom":sQuery(id+"F0.wireOp",EDGE,"E23.2.0.1")}),-1.0]])]});
            extrude(context, id + "F3", {"entities" : qUnion([Q0]), "depth" : 95 * mm, "offsetDistance" : 25 * mm});
        }
        {
            var Q0;
            Q0=makeQuery(id+"F0.imprint","IMPRINT",FACE,{"disambiguationData":[TD([[makeQuery(id+"F0.imprint","IMPRINT",EDGE,{"derivedFrom":sQuery(id+"F0.wireOp",EDGE,"E23.3.0.1")}),-1.0]])]});
            extrude(context, id + "F4", {"entities" : qUnion([Q0]), "depth" : 115 * mm, "offsetDistance" : 25 * mm});
        }
        {
            var Q0;
            Q0=makeQuery(id+"F0.imprint","IMPRINT",FACE,{"disambiguationData":[TD([[makeQuery(id+"F0.imprint","IMPRINT",EDGE,{"derivedFrom":sQuery(id+"F0.wireOp",EDGE,"E23.4.0.1")}),-1.0]])]});
            extrude(context, id + "F5", {"entities" : qUnion([Q0]), "depth" : 135 * mm, "offsetDistance" : 25 * mm});
        }
        {
            var Q0;
            Q0=makeQuery(id+"F0.imprint","IMPRINT",FACE,{"disambiguationData":[TD([[makeQuery(id+"F0.imprint","IMPRINT",EDGE,{"derivedFrom":sQuery(id+"F0.wireOp",EDGE,"E23.5.0.1")}),-1.0]])]});
            extrude(context, id + "F6", {"entities" : qUnion([Q0]), "depth" : 155 * mm, "offsetDistance" : 25 * mm});
        }
        {
            var Q0;
            Q0=makeQuery(id+"F0.imprint","IMPRINT",FACE,{"disambiguationData":[TD([[makeQuery(id+"F0.imprint","IMPRINT",EDGE,{"derivedFrom":sQuery(id+"F0.wireOp",EDGE,"E23.6.0.1")}),-1.0]])]});
            extrude(context, id + "F7", {"entities" : qUnion([Q0]), "depth" : 175 * mm, "offsetDistance" : 25 * mm});
        }
        {
            var Q0;
            Q0=makeQuery(id+"F0.imprint","IMPRINT",FACE,{"disambiguationData":[TD([[makeQuery(id+"F0.imprint","IMPRINT",EDGE,{"derivedFrom":sQuery(id+"F0.wireOp",EDGE,"E24.3.7.0")}),-1.0]])]});
            extrude(context, id + "F8", {"entities" : qUnion([Q0]), "depth" : 195 * mm, "offsetDistance" : 25 * mm});
        }
        {
            var Q0;
            Q0=makeQuery(id+"F0.imprint","IMPRINT",FACE,{"disambiguationData":[TD([[makeQuery(id+"F0.imprint","IMPRINT",EDGE,{"derivedFrom":sQuery(id+"F0.wireOp",EDGE,"E24.3.8.0")}),-1.0]])]});
            extrude(context, id + "F9", {"entities" : qUnion([Q0]), "depth" : 275 * mm, "offsetDistance" : 25 * mm});
        }
        {
            var Q0;
            Q0=makeQuery(id+"F0.imprint","IMPRINT",FACE,{"disambiguationData":[TD([[makeQuery(id+"F0.imprint","IMPRINT",EDGE,{"derivedFrom":sQuery(id+"F0.wireOp",EDGE,"E24.3.9.0")}),-1.0]])]});
            extrude(context, id + "F10", {"entities" : qUnion([Q0]), "depth" : 375 * mm, "offsetDistance" : 25 * mm});
        }
        {
            var Q0;
            Q0=makeQuery(id+"F0.imprint","IMPRINT",FACE,{"disambiguationData":[TD([[makeQuery(id+"F0.imprint","IMPRINT",EDGE,{"derivedFrom":sQuery(id+"F0.wireOp",EDGE,"E24.3.10.0")}),-1.0]])]});
            extrude(context, id + "F11", {"entities" : qUnion([Q0]), "depth" : 995 * mm, "offsetDistance" : 25 * mm});
        }
        {
            var Q0;
            Q0=makeQuery(id+"F1.opExtrude","SWEPT_FACE",FACE,{"disambiguationData":[OSD([sQuery(id+"F0.wireOp",EDGE,"E1.top")])]});
            var sketch = newSketch(context, id + "F12", { "sketchPlane" : qUnion([Q0])});
            skPoint(sketch, "E25", {"position": v(0, -7.5) * mm});
            skPoint(sketch, "E26.1.0.0", {"position": v(15, -7.5) * mm});
            skPoint(sketch, "E26.2.0.0", {"position": v(30, -7.5) * mm});
            skPoint(sketch, "E26.3.0.0", {"position": v(45, -7.5) * mm});
            skPoint(sketch, "E26.4.0.0", {"position": v(60, -7.5) * mm});
            skPoint(sketch, "E26.5.0.0", {"position": v(75, -7.5) * mm});
            skPoint(sketch, "E26.6.0.0", {"position": v(90, -7.5) * mm});
            skLineSegment(sketch, "E26.direction1", {"start": v(0, -7.5) * mm, "end": v(15, -7.5) * mm, "construction": true});
            skPoint(sketch, "E27.1.0.0", {"position": v(0, -27.5) * mm});
            skPoint(sketch, "E27.1.0.1", {"position": v(15, -27.5) * mm});
            skPoint(sketch, "E27.1.0.2", {"position": v(30, -27.5) * mm});
            skPoint(sketch, "E27.1.0.3", {"position": v(45, -27.5) * mm});
            skPoint(sketch, "E27.1.0.4", {"position": v(60, -27.5) * mm});
            skPoint(sketch, "E27.1.0.5", {"position": v(75, -27.5) * mm});
            skPoint(sketch, "E27.1.0.6", {"position": v(90, -27.5) * mm});
            skPoint(sketch, "E27.2.0.0", {"position": v(0, -47.5) * mm});
            skPoint(sketch, "E27.2.0.1", {"position": v(15, -47.5) * mm});
            skPoint(sketch, "E27.2.0.2", {"position": v(30, -47.5) * mm});
            skPoint(sketch, "E27.2.0.3", {"position": v(45, -47.5) * mm});
            skPoint(sketch, "E27.2.0.4", {"position": v(60, -47.5) * mm});
            skPoint(sketch, "E27.2.0.5", {"position": v(75, -47.5) * mm});
            skPoint(sketch, "E27.2.0.6", {"position": v(90, -47.5) * mm});
            skPoint(sketch, "E27.3.0.0", {"position": v(0, -67.5) * mm});
            skPoint(sketch, "E27.3.0.1", {"position": v(15, -67.5) * mm});
            skPoint(sketch, "E27.3.0.2", {"position": v(30, -67.5) * mm});
            skPoint(sketch, "E27.3.0.3", {"position": v(45, -67.5) * mm});
            skPoint(sketch, "E27.3.0.4", {"position": v(60, -67.5) * mm});
            skPoint(sketch, "E27.3.0.5", {"position": v(75, -67.5) * mm});
            skPoint(sketch, "E27.3.0.6", {"position": v(90, -67.5) * mm});
            skPoint(sketch, "E27.4.0.0", {"position": v(0, -87.5) * mm});
            skPoint(sketch, "E27.4.0.1", {"position": v(15, -87.5) * mm});
            skPoint(sketch, "E27.4.0.2", {"position": v(30, -87.5) * mm});
            skPoint(sketch, "E27.4.0.3", {"position": v(45, -87.5) * mm});
            skPoint(sketch, "E27.4.0.4", {"position": v(60, -87.5) * mm});
            skPoint(sketch, "E27.4.0.5", {"position": v(75, -87.5) * mm});
            skPoint(sketch, "E27.4.0.6", {"position": v(90, -87.5) * mm});
            skPoint(sketch, "E27.5.0.0", {"position": v(0, -107.5) * mm});
            skPoint(sketch, "E27.5.0.1", {"position": v(15, -107.5) * mm});
            skPoint(sketch, "E27.5.0.2", {"position": v(30, -107.5) * mm});
            skPoint(sketch, "E27.5.0.3", {"position": v(45, -107.5) * mm});
            skPoint(sketch, "E27.5.0.4", {"position": v(60, -107.5) * mm});
            skPoint(sketch, "E27.5.0.5", {"position": v(75, -107.5) * mm});
            skPoint(sketch, "E27.5.0.6", {"position": v(90, -107.5) * mm});
            skPoint(sketch, "E27.6.0.0", {"position": v(0, -127.5) * mm});
            skPoint(sketch, "E27.6.0.1", {"position": v(15, -127.5) * mm});
            skPoint(sketch, "E27.6.0.2", {"position": v(30, -127.5) * mm});
            skPoint(sketch, "E27.6.0.3", {"position": v(45, -127.5) * mm});
            skPoint(sketch, "E27.6.0.4", {"position": v(60, -127.5) * mm});
            skPoint(sketch, "E27.6.0.5", {"position": v(75, -127.5) * mm});
            skPoint(sketch, "E27.6.0.6", {"position": v(90, -127.5) * mm});
            skPoint(sketch, "E27.7.0.0", {"position": v(0, -147.5) * mm});
            skPoint(sketch, "E27.7.0.1", {"position": v(15, -147.5) * mm});
            skPoint(sketch, "E27.7.0.2", {"position": v(30, -147.5) * mm});
            skPoint(sketch, "E27.7.0.3", {"position": v(45, -147.5) * mm});
            skPoint(sketch, "E27.7.0.4", {"position": v(60, -147.5) * mm});
            skPoint(sketch, "E27.7.0.5", {"position": v(75, -147.5) * mm});
            skPoint(sketch, "E27.7.0.6", {"position": v(90, -147.5) * mm});
            skPoint(sketch, "E27.8.0.0", {"position": v(0, -167.5) * mm});
            skPoint(sketch, "E27.8.0.1", {"position": v(15, -167.5) * mm});
            skPoint(sketch, "E27.8.0.2", {"position": v(30, -167.5) * mm});
            skPoint(sketch, "E27.8.0.3", {"position": v(45, -167.5) * mm});
            skPoint(sketch, "E27.8.0.4", {"position": v(60, -167.5) * mm});
            skPoint(sketch, "E27.8.0.5", {"position": v(75, -167.5) * mm});
            skPoint(sketch, "E27.8.0.6", {"position": v(90, -167.5) * mm});
            skPoint(sketch, "E27.9.0.0", {"position": v(0, -187.5) * mm});
            skPoint(sketch, "E27.9.0.1", {"position": v(15, -187.5) * mm});
            skPoint(sketch, "E27.9.0.2", {"position": v(30, -187.5) * mm});
            skPoint(sketch, "E27.9.0.3", {"position": v(45, -187.5) * mm});
            skPoint(sketch, "E27.9.0.4", {"position": v(60, -187.5) * mm});
            skPoint(sketch, "E27.9.0.5", {"position": v(75, -187.5) * mm});
            skPoint(sketch, "E27.9.0.6", {"position": v(90, -187.5) * mm});
            skLineSegment(sketch, "E27.direction1", {"start": v(0, -7.5) * mm, "end": v(0, -27.5) * mm, "construction": true});
            skPoint(sketch, "E28.0.7.0", {"position": v(105, -7.5) * mm});
            skPoint(sketch, "E28.0.8.0", {"position": v(120, -7.5) * mm});
            skPoint(sketch, "E28.0.9.0", {"position": v(135, -7.5) * mm});
            skPoint(sketch, "E28.0.10.0", {"position": v(150, -7.5) * mm});
            skPoint(sketch, "E29.1.0.0", {"position": v(150, -27.5) * mm});
            skPoint(sketch, "E29.1.0.1", {"position": v(135, -27.5) * mm});
            skPoint(sketch, "E29.1.0.2", {"position": v(120, -27.5) * mm});
            skPoint(sketch, "E29.1.0.3", {"position": v(105, -27.5) * mm});
            skPoint(sketch, "E29.2.0.0", {"position": v(150, -47.5) * mm});
            skPoint(sketch, "E29.2.0.1", {"position": v(135, -47.5) * mm});
            skPoint(sketch, "E29.2.0.2", {"position": v(120, -47.5) * mm});
            skPoint(sketch, "E29.2.0.3", {"position": v(105, -47.5) * mm});
            skLineSegment(sketch, "E29.direction1", {"start": v(105, -7.5) * mm, "end": v(105, -27.5) * mm, "construction": true});
            skPoint(sketch, "E30.0.3.0", {"position": v(150, -67.5) * mm});
            skPoint(sketch, "E30.1.3.0", {"position": v(135, -67.5) * mm});
            skPoint(sketch, "E30.2.3.0", {"position": v(120, -67.5) * mm});
            skPoint(sketch, "E30.3.3.0", {"position": v(105, -67.5) * mm});
            skPoint(sketch, "E30.0.4.0", {"position": v(150, -87.5) * mm});
            skPoint(sketch, "E30.1.4.0", {"position": v(135, -87.5) * mm});
            skPoint(sketch, "E30.2.4.0", {"position": v(120, -87.5) * mm});
            skPoint(sketch, "E30.3.4.0", {"position": v(105, -87.5) * mm});
            skPoint(sketch, "E30.0.5.0", {"position": v(150, -107.5) * mm});
            skPoint(sketch, "E30.1.5.0", {"position": v(135, -107.5) * mm});
            skPoint(sketch, "E30.2.5.0", {"position": v(120, -107.5) * mm});
            skPoint(sketch, "E30.3.5.0", {"position": v(105, -107.5) * mm});
            skPoint(sketch, "E30.0.6.0", {"position": v(150, -127.5) * mm});
            skPoint(sketch, "E30.1.6.0", {"position": v(135, -127.5) * mm});
            skPoint(sketch, "E30.2.6.0", {"position": v(120, -127.5) * mm});
            skPoint(sketch, "E30.3.6.0", {"position": v(105, -127.5) * mm});
            skPoint(sketch, "E30.0.7.0", {"position": v(150, -147.5) * mm});
            skPoint(sketch, "E30.1.7.0", {"position": v(135, -147.5) * mm});
            skPoint(sketch, "E30.2.7.0", {"position": v(120, -147.5) * mm});
            skPoint(sketch, "E30.3.7.0", {"position": v(105, -147.5) * mm});
            skPoint(sketch, "E30.0.8.0", {"position": v(150, -167.5) * mm});
            skPoint(sketch, "E30.1.8.0", {"position": v(135, -167.5) * mm});
            skPoint(sketch, "E30.2.8.0", {"position": v(120, -167.5) * mm});
            skPoint(sketch, "E30.3.8.0", {"position": v(105, -167.5) * mm});
            skPoint(sketch, "E30.0.9.0", {"position": v(150, -187.5) * mm});
            skPoint(sketch, "E30.1.9.0", {"position": v(135, -187.5) * mm});
            skPoint(sketch, "E30.2.9.0", {"position": v(120, -187.5) * mm});
            skPoint(sketch, "E30.3.9.0", {"position": v(105, -187.5) * mm});
            skPoint(sketch, "E30.0.10.0", {"position": v(150, -207.5) * mm});
            skPoint(sketch, "E30.1.10.0", {"position": v(135, -207.5) * mm});
            skPoint(sketch, "E30.2.10.0", {"position": v(120, -207.5) * mm});
            skPoint(sketch, "E30.3.10.0", {"position": v(105, -207.5) * mm});
            skPoint(sketch, "E30.0.11.0", {"position": v(150, -227.5) * mm});
            skPoint(sketch, "E30.1.11.0", {"position": v(135, -227.5) * mm});
            skPoint(sketch, "E30.2.11.0", {"position": v(120, -227.5) * mm});
            skPoint(sketch, "E30.3.11.0", {"position": v(105, -227.5) * mm});
            skPoint(sketch, "E30.0.12.0", {"position": v(150, -247.5) * mm});
            skPoint(sketch, "E30.1.12.0", {"position": v(135, -247.5) * mm});
            skPoint(sketch, "E30.2.12.0", {"position": v(120, -247.5) * mm});
            skPoint(sketch, "E30.3.12.0", {"position": v(105, -247.5) * mm});
            skPoint(sketch, "E30.0.13.0", {"position": v(150, -267.5) * mm});
            skPoint(sketch, "E30.1.13.0", {"position": v(135, -267.5) * mm});
            skPoint(sketch, "E30.2.13.0", {"position": v(120, -267.5) * mm});
            skPoint(sketch, "E30.3.13.0", {"position": v(105, -267.5) * mm});
            skPoint(sketch, "E30.0.14.0", {"position": v(150, -287.5) * mm});
            skPoint(sketch, "E30.1.14.0", {"position": v(135, -287.5) * mm});
            skPoint(sketch, "E30.2.14.0", {"position": v(120, -287.5) * mm});
            skPoint(sketch, "E30.3.14.0", {"position": v(105, -287.5) * mm});
            skPoint(sketch, "E30.0.15.0", {"position": v(150, -307.5) * mm});
            skPoint(sketch, "E30.1.15.0", {"position": v(135, -307.5) * mm});
            skPoint(sketch, "E30.2.15.0", {"position": v(120, -307.5) * mm});
            skPoint(sketch, "E30.3.15.0", {"position": v(105, -307.5) * mm});
            skPoint(sketch, "E30.0.16.0", {"position": v(150, -327.5) * mm});
            skPoint(sketch, "E30.1.16.0", {"position": v(135, -327.5) * mm});
            skPoint(sketch, "E30.2.16.0", {"position": v(120, -327.5) * mm});
            skPoint(sketch, "E30.3.16.0", {"position": v(105, -327.5) * mm});
            skPoint(sketch, "E30.0.17.0", {"position": v(150, -347.5) * mm});
            skPoint(sketch, "E30.1.17.0", {"position": v(135, -347.5) * mm});
            skPoint(sketch, "E30.2.17.0", {"position": v(120, -347.5) * mm});
            skPoint(sketch, "E30.3.17.0", {"position": v(105, -347.5) * mm});
            skPoint(sketch, "E30.0.18.0", {"position": v(150, -367.5) * mm});
            skPoint(sketch, "E30.1.18.0", {"position": v(135, -367.5) * mm});
            skPoint(sketch, "E30.2.18.0", {"position": v(120, -367.5) * mm});
            skPoint(sketch, "E30.3.18.0", {"position": v(105, -367.5) * mm});
            skPoint(sketch, "E30.0.19.0", {"position": v(150, -387.5) * mm});
            skPoint(sketch, "E30.1.19.0", {"position": v(135, -387.5) * mm});
            skPoint(sketch, "E30.2.19.0", {"position": v(120, -387.5) * mm});
            skPoint(sketch, "E30.3.19.0", {"position": v(105, -387.5) * mm});
            skPoint(sketch, "E30.0.20.0", {"position": v(150, -407.5) * mm});
            skPoint(sketch, "E30.1.20.0", {"position": v(135, -407.5) * mm});
            skPoint(sketch, "E30.2.20.0", {"position": v(120, -407.5) * mm});
            skPoint(sketch, "E30.3.20.0", {"position": v(105, -407.5) * mm});
            skPoint(sketch, "E30.0.21.0", {"position": v(150, -427.5) * mm});
            skPoint(sketch, "E30.1.21.0", {"position": v(135, -427.5) * mm});
            skPoint(sketch, "E30.2.21.0", {"position": v(120, -427.5) * mm});
            skPoint(sketch, "E30.3.21.0", {"position": v(105, -427.5) * mm});
            skPoint(sketch, "E30.0.22.0", {"position": v(150, -447.5) * mm});
            skPoint(sketch, "E30.1.22.0", {"position": v(135, -447.5) * mm});
            skPoint(sketch, "E30.2.22.0", {"position": v(120, -447.5) * mm});
            skPoint(sketch, "E30.3.22.0", {"position": v(105, -447.5) * mm});
            skPoint(sketch, "E30.0.23.0", {"position": v(150, -467.5) * mm});
            skPoint(sketch, "E30.1.23.0", {"position": v(135, -467.5) * mm});
            skPoint(sketch, "E30.2.23.0", {"position": v(120, -467.5) * mm});
            skPoint(sketch, "E30.3.23.0", {"position": v(105, -467.5) * mm});
            skPoint(sketch, "E30.0.24.0", {"position": v(150, -487.5) * mm});
            skPoint(sketch, "E30.1.24.0", {"position": v(135, -487.5) * mm});
            skPoint(sketch, "E30.2.24.0", {"position": v(120, -487.5) * mm});
            skPoint(sketch, "E30.3.24.0", {"position": v(105, -487.5) * mm});
            skPoint(sketch, "E30.0.25.0", {"position": v(150, -507.5) * mm});
            skPoint(sketch, "E30.1.25.0", {"position": v(135, -507.5) * mm});
            skPoint(sketch, "E30.2.25.0", {"position": v(120, -507.5) * mm});
            skPoint(sketch, "E30.3.25.0", {"position": v(105, -507.5) * mm});
            skPoint(sketch, "E30.0.26.0", {"position": v(150, -527.5) * mm});
            skPoint(sketch, "E30.1.26.0", {"position": v(135, -527.5) * mm});
            skPoint(sketch, "E30.2.26.0", {"position": v(120, -527.5) * mm});
            skPoint(sketch, "E30.3.26.0", {"position": v(105, -527.5) * mm});
            skPoint(sketch, "E30.0.27.0", {"position": v(150, -547.5) * mm});
            skPoint(sketch, "E30.1.27.0", {"position": v(135, -547.5) * mm});
            skPoint(sketch, "E30.2.27.0", {"position": v(120, -547.5) * mm});
            skPoint(sketch, "E30.3.27.0", {"position": v(105, -547.5) * mm});
            skPoint(sketch, "E30.0.28.0", {"position": v(150, -567.5) * mm});
            skPoint(sketch, "E30.1.28.0", {"position": v(135, -567.5) * mm});
            skPoint(sketch, "E30.2.28.0", {"position": v(120, -567.5) * mm});
            skPoint(sketch, "E30.3.28.0", {"position": v(105, -567.5) * mm});
            skPoint(sketch, "E30.0.29.0", {"position": v(150, -587.5) * mm});
            skPoint(sketch, "E30.1.29.0", {"position": v(135, -587.5) * mm});
            skPoint(sketch, "E30.2.29.0", {"position": v(120, -587.5) * mm});
            skPoint(sketch, "E30.3.29.0", {"position": v(105, -587.5) * mm});
            skPoint(sketch, "E30.0.30.0", {"position": v(150, -607.5) * mm});
            skPoint(sketch, "E30.1.30.0", {"position": v(135, -607.5) * mm});
            skPoint(sketch, "E30.2.30.0", {"position": v(120, -607.5) * mm});
            skPoint(sketch, "E30.3.30.0", {"position": v(105, -607.5) * mm});
            skPoint(sketch, "E30.0.31.0", {"position": v(150, -627.5) * mm});
            skPoint(sketch, "E30.1.31.0", {"position": v(135, -627.5) * mm});
            skPoint(sketch, "E30.2.31.0", {"position": v(120, -627.5) * mm});
            skPoint(sketch, "E30.3.31.0", {"position": v(105, -627.5) * mm});
            skPoint(sketch, "E30.0.32.0", {"position": v(150, -647.5) * mm});
            skPoint(sketch, "E30.1.32.0", {"position": v(135, -647.5) * mm});
            skPoint(sketch, "E30.2.32.0", {"position": v(120, -647.5) * mm});
            skPoint(sketch, "E30.3.32.0", {"position": v(105, -647.5) * mm});
            skPoint(sketch, "E30.0.33.0", {"position": v(150, -667.5) * mm});
            skPoint(sketch, "E30.1.33.0", {"position": v(135, -667.5) * mm});
            skPoint(sketch, "E30.2.33.0", {"position": v(120, -667.5) * mm});
            skPoint(sketch, "E30.3.33.0", {"position": v(105, -667.5) * mm});
            skPoint(sketch, "E30.0.34.0", {"position": v(150, -687.5) * mm});
            skPoint(sketch, "E30.1.34.0", {"position": v(135, -687.5) * mm});
            skPoint(sketch, "E30.2.34.0", {"position": v(120, -687.5) * mm});
            skPoint(sketch, "E30.3.34.0", {"position": v(105, -687.5) * mm});
            skPoint(sketch, "E30.0.35.0", {"position": v(150, -707.5) * mm});
            skPoint(sketch, "E30.1.35.0", {"position": v(135, -707.5) * mm});
            skPoint(sketch, "E30.2.35.0", {"position": v(120, -707.5) * mm});
            skPoint(sketch, "E30.3.35.0", {"position": v(105, -707.5) * mm});
            skPoint(sketch, "E30.0.36.0", {"position": v(150, -727.5) * mm});
            skPoint(sketch, "E30.1.36.0", {"position": v(135, -727.5) * mm});
            skPoint(sketch, "E30.2.36.0", {"position": v(120, -727.5) * mm});
            skPoint(sketch, "E30.3.36.0", {"position": v(105, -727.5) * mm});
            skPoint(sketch, "E30.0.37.0", {"position": v(150, -747.5) * mm});
            skPoint(sketch, "E30.1.37.0", {"position": v(135, -747.5) * mm});
            skPoint(sketch, "E30.2.37.0", {"position": v(120, -747.5) * mm});
            skPoint(sketch, "E30.3.37.0", {"position": v(105, -747.5) * mm});
            skPoint(sketch, "E30.0.38.0", {"position": v(150, -767.5) * mm});
            skPoint(sketch, "E30.1.38.0", {"position": v(135, -767.5) * mm});
            skPoint(sketch, "E30.2.38.0", {"position": v(120, -767.5) * mm});
            skPoint(sketch, "E30.3.38.0", {"position": v(105, -767.5) * mm});
            skPoint(sketch, "E30.0.39.0", {"position": v(150, -787.5) * mm});
            skPoint(sketch, "E30.1.39.0", {"position": v(135, -787.5) * mm});
            skPoint(sketch, "E30.2.39.0", {"position": v(120, -787.5) * mm});
            skPoint(sketch, "E30.3.39.0", {"position": v(105, -787.5) * mm});
            skPoint(sketch, "E31.0.40.0", {"position": v(150, -807.5) * mm});
            skPoint(sketch, "E31.1.40.0", {"position": v(135, -807.5) * mm});
            skPoint(sketch, "E31.2.40.0", {"position": v(120, -807.5) * mm});
            skPoint(sketch, "E31.3.40.0", {"position": v(105, -807.5) * mm});
            skPoint(sketch, "E31.0.41.0", {"position": v(150, -827.5) * mm});
            skPoint(sketch, "E31.1.41.0", {"position": v(135, -827.5) * mm});
            skPoint(sketch, "E31.2.41.0", {"position": v(120, -827.5) * mm});
            skPoint(sketch, "E31.3.41.0", {"position": v(105, -827.5) * mm});
            skPoint(sketch, "E31.0.42.0", {"position": v(150, -847.5) * mm});
            skPoint(sketch, "E31.1.42.0", {"position": v(135, -847.5) * mm});
            skPoint(sketch, "E31.2.42.0", {"position": v(120, -847.5) * mm});
            skPoint(sketch, "E31.3.42.0", {"position": v(105, -847.5) * mm});
            skPoint(sketch, "E31.0.43.0", {"position": v(150, -867.5) * mm});
            skPoint(sketch, "E31.1.43.0", {"position": v(135, -867.5) * mm});
            skPoint(sketch, "E31.2.43.0", {"position": v(120, -867.5) * mm});
            skPoint(sketch, "E31.3.43.0", {"position": v(105, -867.5) * mm});
            skPoint(sketch, "E31.0.44.0", {"position": v(150, -887.5) * mm});
            skPoint(sketch, "E31.1.44.0", {"position": v(135, -887.5) * mm});
            skPoint(sketch, "E31.2.44.0", {"position": v(120, -887.5) * mm});
            skPoint(sketch, "E31.3.44.0", {"position": v(105, -887.5) * mm});
            skPoint(sketch, "E31.0.45.0", {"position": v(150, -907.5) * mm});
            skPoint(sketch, "E31.1.45.0", {"position": v(135, -907.5) * mm});
            skPoint(sketch, "E31.2.45.0", {"position": v(120, -907.5) * mm});
            skPoint(sketch, "E31.3.45.0", {"position": v(105, -907.5) * mm});
            skPoint(sketch, "E31.0.46.0", {"position": v(150, -927.5) * mm});
            skPoint(sketch, "E31.1.46.0", {"position": v(135, -927.5) * mm});
            skPoint(sketch, "E31.2.46.0", {"position": v(120, -927.5) * mm});
            skPoint(sketch, "E31.3.46.0", {"position": v(105, -927.5) * mm});
            skPoint(sketch, "E31.0.47.0", {"position": v(150, -947.5) * mm});
            skPoint(sketch, "E31.1.47.0", {"position": v(135, -947.5) * mm});
            skPoint(sketch, "E31.2.47.0", {"position": v(120, -947.5) * mm});
            skPoint(sketch, "E31.3.47.0", {"position": v(105, -947.5) * mm});
            skPoint(sketch, "E31.0.48.0", {"position": v(150, -967.5) * mm});
            skPoint(sketch, "E31.1.48.0", {"position": v(135, -967.5) * mm});
            skPoint(sketch, "E31.2.48.0", {"position": v(120, -967.5) * mm});
            skPoint(sketch, "E31.3.48.0", {"position": v(105, -967.5) * mm});
            skPoint(sketch, "E31.0.49.0", {"position": v(150, -987.5) * mm});
            skPoint(sketch, "E31.1.49.0", {"position": v(135, -987.5) * mm});
            skPoint(sketch, "E31.2.49.0", {"position": v(120, -987.5) * mm});
            skPoint(sketch, "E31.3.49.0", {"position": v(105, -987.5) * mm});
            skSolve(sketch);
        }
        {
            var Q0;
            Q0=sQuery(id+"F12.wireOp",VERTEX,"E26.5.0.0");
            var Q1;
            Q1=sQuery(id+"F12.wireOp",VERTEX,"E29.2.0.1");
            var Q2;
            Q2=sQuery(id+"F12.wireOp",VERTEX,"E27.2.0.1");
            var Q3;
            Q3=sQuery(id+"F12.wireOp",VERTEX,"E26.4.0.0");
            var Q4;
            Q4=sQuery(id+"F12.wireOp",VERTEX,"E27.1.0.6");
            var Q5;
            Q5=sQuery(id+"F12.wireOp",VERTEX,"E27.2.0.6");
            var Q6;
            Q6=sQuery(id+"F12.wireOp",VERTEX,"E29.1.0.2");
            var Q7;
            Q7=sQuery(id+"F12.wireOp",VERTEX,"E26.2.0.0");
            var Q8;
            Q8=sQuery(id+"F12.wireOp",VERTEX,"E28.0.7.0");
            var Q9;
            Q9=sQuery(id+"F12.wireOp",VERTEX,"E27.2.0.2");
            var Q10;
            Q10=sQuery(id+"F12.wireOp",VERTEX,"E27.2.0.0");
            var Q11;
            Q11=sQuery(id+"F12.wireOp",VERTEX,"E27.2.0.5");
            var Q12;
            Q12=sQuery(id+"F12.wireOp",VERTEX,"E26.3.0.0");
            var Q13;
            Q13=sQuery(id+"F12.wireOp",VERTEX,"E26.6.0.0");
            var Q14;
            Q14=sQuery(id+"F12.wireOp",VERTEX,"E29.2.0.2");
            var Q15;
            Q15=sQuery(id+"F12.wireOp",VERTEX,"E29.1.0.3");
            var Q16;
            Q16=sQuery(id+"F12.wireOp",VERTEX,"E26.1.0.0");
            var Q17;
            Q17=sQuery(id+"F12.wireOp",VERTEX,"E29.2.0.3");
            var Q18;
            Q18=sQuery(id+"F12.wireOp",VERTEX,"E27.1.0.5");
            var Q19;
            Q19=sQuery(id+"F12.wireOp",VERTEX,"E29.1.0.1");
            var Q20;
            Q20=sQuery(id+"F12.wireOp",VERTEX,"E27.2.0.3");
            var Q21;
            Q21=sQuery(id+"F12.wireOp",VERTEX,"E25");
            var Q22;
            Q22=sQuery(id+"F12.wireOp",VERTEX,"E27.2.0.4");
            var Q23;
            Q23=sQuery(id+"F12.wireOp",VERTEX,"E27.1.0.2");
            var Q24;
            Q24=sQuery(id+"F12.wireOp",VERTEX,"E28.0.8.0");
            var Q25;
            Q25=sQuery(id+"F12.wireOp",VERTEX,"E27.1.0.3");
            var Q26;
            Q26=sQuery(id+"F12.wireOp",VERTEX,"E28.0.9.0");
            var Q27;
            Q27=sQuery(id+"F12.wireOp",VERTEX,"E27.1.0.4");
            var Q28;
            Q28=sQuery(id+"F12.wireOp",VERTEX,"E27.1.0.0");
            var Q29;
            Q29=sQuery(id+"F12.wireOp",VERTEX,"E27.1.0.1");
            var Q30;
            Q30=sQuery(id+"F12.wireOp",VERTEX,"E30.1.3.0");
            var Q31;
            Q31=sQuery(id+"F12.wireOp",VERTEX,"E27.3.0.2");
            var Q32;
            Q32=sQuery(id+"F12.wireOp",VERTEX,"E30.2.3.0");
            var Q33;
            Q33=sQuery(id+"F12.wireOp",VERTEX,"E27.3.0.3");
            var Q34;
            Q34=sQuery(id+"F12.wireOp",VERTEX,"E27.3.0.1");
            var Q35;
            Q35=sQuery(id+"F12.wireOp",VERTEX,"E30.3.3.0");
            var Q36;
            Q36=sQuery(id+"F12.wireOp",VERTEX,"E27.3.0.4");
            var Q37;
            Q37=sQuery(id+"F12.wireOp",VERTEX,"E27.3.0.5");
            var Q38;
            Q38=sQuery(id+"F12.wireOp",VERTEX,"E27.3.0.6");
            var Q39;
            Q39=sQuery(id+"F12.wireOp",VERTEX,"E27.4.0.2");
            var Q40;
            Q40=sQuery(id+"F12.wireOp",VERTEX,"E27.4.0.3");
            var Q41;
            Q41=sQuery(id+"F12.wireOp",VERTEX,"E27.4.0.5");
            var Q42;
            Q42=sQuery(id+"F12.wireOp",VERTEX,"E27.4.0.4");
            var Q43;
            Q43=sQuery(id+"F12.wireOp",VERTEX,"E30.3.4.0");
            var Q44;
            Q44=sQuery(id+"F12.wireOp",VERTEX,"E27.4.0.6");
            var Q45;
            Q45=sQuery(id+"F12.wireOp",VERTEX,"E30.1.4.0");
            var Q46;
            Q46=sQuery(id+"F12.wireOp",VERTEX,"E30.2.4.0");
            var Q47;
            Q47=sQuery(id+"F12.wireOp",VERTEX,"E27.5.0.5");
            var Q48;
            Q48=sQuery(id+"F12.wireOp",VERTEX,"E27.5.0.3");
            var Q49;
            Q49=sQuery(id+"F12.wireOp",VERTEX,"E27.5.0.4");
            var Q50;
            Q50=sQuery(id+"F12.wireOp",VERTEX,"E30.1.5.0");
            var Q51;
            Q51=sQuery(id+"F12.wireOp",VERTEX,"E30.3.5.0");
            var Q52;
            Q52=sQuery(id+"F12.wireOp",VERTEX,"E30.2.5.0");
            var Q53;
            Q53=sQuery(id+"F12.wireOp",VERTEX,"E27.5.0.6");
            var Q54;
            Q54=sQuery(id+"F12.wireOp",VERTEX,"E30.1.6.0");
            var Q55;
            Q55=sQuery(id+"F12.wireOp",VERTEX,"E30.3.6.0");
            var Q56;
            Q56=sQuery(id+"F12.wireOp",VERTEX,"E30.2.6.0");
            var Q57;
            Q57=sQuery(id+"F12.wireOp",VERTEX,"E27.6.0.4");
            var Q58;
            Q58=sQuery(id+"F12.wireOp",VERTEX,"E27.6.0.5");
            var Q59;
            Q59=sQuery(id+"F12.wireOp",VERTEX,"E27.6.0.6");
            var Q60;
            Q60=sQuery(id+"F12.wireOp",VERTEX,"E27.7.0.5");
            var Q61;
            Q61=sQuery(id+"F12.wireOp",VERTEX,"E27.7.0.6");
            var Q62;
            Q62=sQuery(id+"F12.wireOp",VERTEX,"E30.2.7.0");
            var Q63;
            Q63=sQuery(id+"F12.wireOp",VERTEX,"E30.3.7.0");
            var Q64;
            Q64=sQuery(id+"F12.wireOp",VERTEX,"E30.1.7.0");
            var Q65;
            Q65=sQuery(id+"F12.wireOp",VERTEX,"E27.8.0.6");
            var Q66;
            Q66=sQuery(id+"F12.wireOp",VERTEX,"E30.3.8.0");
            var Q67;
            Q67=sQuery(id+"F12.wireOp",VERTEX,"E30.1.8.0");
            var Q68;
            Q68=sQuery(id+"F12.wireOp",VERTEX,"E30.2.8.0");
            var Q69;
            Q69=sQuery(id+"F12.wireOp",VERTEX,"E30.1.9.0");
            var Q70;
            Q70=sQuery(id+"F12.wireOp",VERTEX,"E30.3.9.0");
            var Q71;
            Q71=sQuery(id+"F12.wireOp",VERTEX,"E30.2.9.0");
            var Q72;
            Q72=sQuery(id+"F12.wireOp",VERTEX,"E30.2.11.0");
            var Q73;
            Q73=sQuery(id+"F12.wireOp",VERTEX,"E30.1.13.0");
            var Q74;
            Q74=sQuery(id+"F12.wireOp",VERTEX,"E30.1.11.0");
            var Q75;
            Q75=sQuery(id+"F12.wireOp",VERTEX,"E30.2.13.0");
            var Q76;
            Q76=sQuery(id+"F12.wireOp",VERTEX,"E30.2.10.0");
            var Q77;
            Q77=sQuery(id+"F12.wireOp",VERTEX,"E30.1.10.0");
            var Q78;
            Q78=sQuery(id+"F12.wireOp",VERTEX,"E30.1.12.0");
            var Q79;
            Q79=sQuery(id+"F12.wireOp",VERTEX,"E30.2.12.0");
            var Q80;
            Q80=sQuery(id+"F12.wireOp",VERTEX,"E30.1.15.0");
            var Q81;
            Q81=sQuery(id+"F12.wireOp",VERTEX,"E30.1.17.0");
            var Q82;
            Q82=sQuery(id+"F12.wireOp",VERTEX,"E30.1.18.0");
            var Q83;
            Q83=sQuery(id+"F12.wireOp",VERTEX,"E30.1.16.0");
            var Q84;
            Q84=sQuery(id+"F12.wireOp",VERTEX,"E30.1.14.0");
            var Q85;
            Q85=makeQuery(id+"F6.opExtrude","SWEPT_BODY",BODY,{"disambiguationData":[OSD([sQuery(id+"F0.wireOp",EDGE,"E23.5.0.1"),sQuery(id+"F0.wireOp",EDGE,"E23.5.0.2"),sQuery(id+"F0.wireOp",EDGE,"E23.5.0.3"),sQuery(id+"F0.wireOp",EDGE,"E23.5.0.4"),sQuery(id+"F0.wireOp",EDGE,"E23.5.0.11"),sQuery(id+"F0.wireOp",EDGE,"E23.5.0.12"),sQuery(id+"F0.wireOp",EDGE,"E23.5.0.13"),sQuery(id+"F0.wireOp",EDGE,"E23.5.0.14"),sQuery(id+"F0.wireOp",EDGE,"E23.5.0.15"),sQuery(id+"F0.wireOp",EDGE,"E23.5.0.16"),sQuery(id+"F0.wireOp",EDGE,"E23.5.0.18"),sQuery(id+"F0.wireOp",EDGE,"E23.5.0.19"),sQuery(id+"F0.wireOp",EDGE,"E23.5.0.20"),sQuery(id+"F0.wireOp",EDGE,"E23.5.0.21"),sQuery(id+"F0.wireOp",EDGE,"E23.5.0.22"),sQuery(id+"F0.wireOp",EDGE,"E23.5.0.23"),sQuery(id+"F0.wireOp",EDGE,"E23.5.0.24"),sQuery(id+"F0.wireOp",EDGE,"E23.5.0.25"),sQuery(id+"F0.wireOp",EDGE,"E23.5.0.26"),sQuery(id+"F0.wireOp",EDGE,"E23.5.0.27")])]});
            var Q86;
            Q86=makeQuery(id+"F10.opExtrude","SWEPT_BODY",BODY,{"disambiguationData":[OSD([sQuery(id+"F0.wireOp",EDGE,"E24.3.9.0"),sQuery(id+"F0.wireOp",EDGE,"E24.6.9.0"),sQuery(id+"F0.wireOp",EDGE,"E24.9.9.0"),sQuery(id+"F0.wireOp",EDGE,"E24.12.9.0"),sQuery(id+"F0.wireOp",EDGE,"E24.21.9.0"),sQuery(id+"F0.wireOp",EDGE,"E24.24.9.0"),sQuery(id+"F0.wireOp",EDGE,"E24.27.9.0"),sQuery(id+"F0.wireOp",EDGE,"E24.30.9.0"),sQuery(id+"F0.wireOp",EDGE,"E24.33.9.0"),sQuery(id+"F0.wireOp",EDGE,"E24.36.9.0"),sQuery(id+"F0.wireOp",EDGE,"E24.43.9.0"),sQuery(id+"F0.wireOp",EDGE,"E24.46.9.0"),sQuery(id+"F0.wireOp",EDGE,"E24.49.9.0"),sQuery(id+"F0.wireOp",EDGE,"E24.52.9.0"),sQuery(id+"F0.wireOp",EDGE,"E24.56.9.0"),sQuery(id+"F0.wireOp",EDGE,"E24.59.9.0"),sQuery(id+"F0.wireOp",EDGE,"E24.63.9.0"),sQuery(id+"F0.wireOp",EDGE,"E24.66.9.0"),sQuery(id+"F0.wireOp",EDGE,"E24.70.9.0"),sQuery(id+"F0.wireOp",EDGE,"E24.74.9.0")])]});
            var Q87;
            Q87=makeQuery(id+"F2.opExtrude","SWEPT_BODY",BODY,{"disambiguationData":[OSD([sQuery(id+"F0.wireOp",EDGE,"E23.1.0.1"),sQuery(id+"F0.wireOp",EDGE,"E23.1.0.2"),sQuery(id+"F0.wireOp",EDGE,"E23.1.0.3"),sQuery(id+"F0.wireOp",EDGE,"E23.1.0.4"),sQuery(id+"F0.wireOp",EDGE,"E23.1.0.11"),sQuery(id+"F0.wireOp",EDGE,"E23.1.0.12"),sQuery(id+"F0.wireOp",EDGE,"E23.1.0.13"),sQuery(id+"F0.wireOp",EDGE,"E23.1.0.14"),sQuery(id+"F0.wireOp",EDGE,"E23.1.0.15"),sQuery(id+"F0.wireOp",EDGE,"E23.1.0.16"),sQuery(id+"F0.wireOp",EDGE,"E23.1.0.18"),sQuery(id+"F0.wireOp",EDGE,"E23.1.0.19"),sQuery(id+"F0.wireOp",EDGE,"E23.1.0.20"),sQuery(id+"F0.wireOp",EDGE,"E23.1.0.21"),sQuery(id+"F0.wireOp",EDGE,"E23.1.0.22"),sQuery(id+"F0.wireOp",EDGE,"E23.1.0.23"),sQuery(id+"F0.wireOp",EDGE,"E23.1.0.24"),sQuery(id+"F0.wireOp",EDGE,"E23.1.0.25"),sQuery(id+"F0.wireOp",EDGE,"E23.1.0.26"),sQuery(id+"F0.wireOp",EDGE,"E23.1.0.27")])]});
            var Q88;
            Q88=makeQuery(id+"F5.opExtrude","SWEPT_BODY",BODY,{"disambiguationData":[OSD([sQuery(id+"F0.wireOp",EDGE,"E23.4.0.1"),sQuery(id+"F0.wireOp",EDGE,"E23.4.0.2"),sQuery(id+"F0.wireOp",EDGE,"E23.4.0.3"),sQuery(id+"F0.wireOp",EDGE,"E23.4.0.4"),sQuery(id+"F0.wireOp",EDGE,"E23.4.0.11"),sQuery(id+"F0.wireOp",EDGE,"E23.4.0.12"),sQuery(id+"F0.wireOp",EDGE,"E23.4.0.13"),sQuery(id+"F0.wireOp",EDGE,"E23.4.0.14"),sQuery(id+"F0.wireOp",EDGE,"E23.4.0.15"),sQuery(id+"F0.wireOp",EDGE,"E23.4.0.16"),sQuery(id+"F0.wireOp",EDGE,"E23.4.0.18"),sQuery(id+"F0.wireOp",EDGE,"E23.4.0.19"),sQuery(id+"F0.wireOp",EDGE,"E23.4.0.20"),sQuery(id+"F0.wireOp",EDGE,"E23.4.0.21"),sQuery(id+"F0.wireOp",EDGE,"E23.4.0.22"),sQuery(id+"F0.wireOp",EDGE,"E23.4.0.23"),sQuery(id+"F0.wireOp",EDGE,"E23.4.0.24"),sQuery(id+"F0.wireOp",EDGE,"E23.4.0.25"),sQuery(id+"F0.wireOp",EDGE,"E23.4.0.26"),sQuery(id+"F0.wireOp",EDGE,"E23.4.0.27")])]});
            var Q89;
            Q89=makeQuery(id+"F11.opExtrude","SWEPT_BODY",BODY,{"disambiguationData":[OSD([sQuery(id+"F0.wireOp",EDGE,"E24.3.10.0"),sQuery(id+"F0.wireOp",EDGE,"E24.6.10.0"),sQuery(id+"F0.wireOp",EDGE,"E24.9.10.0"),sQuery(id+"F0.wireOp",EDGE,"E24.12.10.0"),sQuery(id+"F0.wireOp",EDGE,"E24.21.10.0"),sQuery(id+"F0.wireOp",EDGE,"E24.24.10.0"),sQuery(id+"F0.wireOp",EDGE,"E24.27.10.0"),sQuery(id+"F0.wireOp",EDGE,"E24.30.10.0"),sQuery(id+"F0.wireOp",EDGE,"E24.33.10.0"),sQuery(id+"F0.wireOp",EDGE,"E24.36.10.0"),sQuery(id+"F0.wireOp",EDGE,"E24.43.10.0"),sQuery(id+"F0.wireOp",EDGE,"E24.46.10.0"),sQuery(id+"F0.wireOp",EDGE,"E24.49.10.0"),sQuery(id+"F0.wireOp",EDGE,"E24.52.10.0"),sQuery(id+"F0.wireOp",EDGE,"E24.56.10.0"),sQuery(id+"F0.wireOp",EDGE,"E24.59.10.0"),sQuery(id+"F0.wireOp",EDGE,"E24.63.10.0"),sQuery(id+"F0.wireOp",EDGE,"E24.66.10.0"),sQuery(id+"F0.wireOp",EDGE,"E24.70.10.0"),sQuery(id+"F0.wireOp",EDGE,"E24.74.10.0")])]});
            var Q90;
            Q90=makeQuery(id+"F7.opExtrude","SWEPT_BODY",BODY,{"disambiguationData":[OSD([sQuery(id+"F0.wireOp",EDGE,"E23.6.0.1"),sQuery(id+"F0.wireOp",EDGE,"E23.6.0.2"),sQuery(id+"F0.wireOp",EDGE,"E23.6.0.3"),sQuery(id+"F0.wireOp",EDGE,"E23.6.0.4"),sQuery(id+"F0.wireOp",EDGE,"E23.6.0.11"),sQuery(id+"F0.wireOp",EDGE,"E23.6.0.12"),sQuery(id+"F0.wireOp",EDGE,"E23.6.0.13"),sQuery(id+"F0.wireOp",EDGE,"E23.6.0.14"),sQuery(id+"F0.wireOp",EDGE,"E23.6.0.15"),sQuery(id+"F0.wireOp",EDGE,"E23.6.0.16"),sQuery(id+"F0.wireOp",EDGE,"E23.6.0.18"),sQuery(id+"F0.wireOp",EDGE,"E23.6.0.19"),sQuery(id+"F0.wireOp",EDGE,"E23.6.0.20"),sQuery(id+"F0.wireOp",EDGE,"E23.6.0.21"),sQuery(id+"F0.wireOp",EDGE,"E23.6.0.22"),sQuery(id+"F0.wireOp",EDGE,"E23.6.0.23"),sQuery(id+"F0.wireOp",EDGE,"E23.6.0.24"),sQuery(id+"F0.wireOp",EDGE,"E23.6.0.25"),sQuery(id+"F0.wireOp",EDGE,"E23.6.0.26"),sQuery(id+"F0.wireOp",EDGE,"E23.6.0.27")])]});
            var Q91;
            Q91=makeQuery(id+"F9.opExtrude","SWEPT_BODY",BODY,{"disambiguationData":[OSD([sQuery(id+"F0.wireOp",EDGE,"E24.3.8.0"),sQuery(id+"F0.wireOp",EDGE,"E24.6.8.0"),sQuery(id+"F0.wireOp",EDGE,"E24.9.8.0"),sQuery(id+"F0.wireOp",EDGE,"E24.12.8.0"),sQuery(id+"F0.wireOp",EDGE,"E24.21.8.0"),sQuery(id+"F0.wireOp",EDGE,"E24.24.8.0"),sQuery(id+"F0.wireOp",EDGE,"E24.27.8.0"),sQuery(id+"F0.wireOp",EDGE,"E24.30.8.0"),sQuery(id+"F0.wireOp",EDGE,"E24.33.8.0"),sQuery(id+"F0.wireOp",EDGE,"E24.36.8.0"),sQuery(id+"F0.wireOp",EDGE,"E24.43.8.0"),sQuery(id+"F0.wireOp",EDGE,"E24.46.8.0"),sQuery(id+"F0.wireOp",EDGE,"E24.49.8.0"),sQuery(id+"F0.wireOp",EDGE,"E24.52.8.0"),sQuery(id+"F0.wireOp",EDGE,"E24.56.8.0"),sQuery(id+"F0.wireOp",EDGE,"E24.59.8.0"),sQuery(id+"F0.wireOp",EDGE,"E24.63.8.0"),sQuery(id+"F0.wireOp",EDGE,"E24.66.8.0"),sQuery(id+"F0.wireOp",EDGE,"E24.70.8.0"),sQuery(id+"F0.wireOp",EDGE,"E24.74.8.0")])]});
            var Q92;
            Q92=makeQuery(id+"F3.opExtrude","SWEPT_BODY",BODY,{"disambiguationData":[OSD([sQuery(id+"F0.wireOp",EDGE,"E23.2.0.1"),sQuery(id+"F0.wireOp",EDGE,"E23.2.0.2"),sQuery(id+"F0.wireOp",EDGE,"E23.2.0.3"),sQuery(id+"F0.wireOp",EDGE,"E23.2.0.4"),sQuery(id+"F0.wireOp",EDGE,"E23.2.0.11"),sQuery(id+"F0.wireOp",EDGE,"E23.2.0.12"),sQuery(id+"F0.wireOp",EDGE,"E23.2.0.13"),sQuery(id+"F0.wireOp",EDGE,"E23.2.0.14"),sQuery(id+"F0.wireOp",EDGE,"E23.2.0.15"),sQuery(id+"F0.wireOp",EDGE,"E23.2.0.16"),sQuery(id+"F0.wireOp",EDGE,"E23.2.0.18"),sQuery(id+"F0.wireOp",EDGE,"E23.2.0.19"),sQuery(id+"F0.wireOp",EDGE,"E23.2.0.20"),sQuery(id+"F0.wireOp",EDGE,"E23.2.0.21"),sQuery(id+"F0.wireOp",EDGE,"E23.2.0.22"),sQuery(id+"F0.wireOp",EDGE,"E23.2.0.23"),sQuery(id+"F0.wireOp",EDGE,"E23.2.0.24"),sQuery(id+"F0.wireOp",EDGE,"E23.2.0.25"),sQuery(id+"F0.wireOp",EDGE,"E23.2.0.26"),sQuery(id+"F0.wireOp",EDGE,"E23.2.0.27")])]});
            var Q93;
            Q93=makeQuery(id+"F8.opExtrude","SWEPT_BODY",BODY,{"disambiguationData":[OSD([sQuery(id+"F0.wireOp",EDGE,"E24.3.7.0"),sQuery(id+"F0.wireOp",EDGE,"E24.6.7.0"),sQuery(id+"F0.wireOp",EDGE,"E24.9.7.0"),sQuery(id+"F0.wireOp",EDGE,"E24.12.7.0"),sQuery(id+"F0.wireOp",EDGE,"E24.21.7.0"),sQuery(id+"F0.wireOp",EDGE,"E24.24.7.0"),sQuery(id+"F0.wireOp",EDGE,"E24.27.7.0"),sQuery(id+"F0.wireOp",EDGE,"E24.30.7.0"),sQuery(id+"F0.wireOp",EDGE,"E24.33.7.0"),sQuery(id+"F0.wireOp",EDGE,"E24.36.7.0"),sQuery(id+"F0.wireOp",EDGE,"E24.43.7.0"),sQuery(id+"F0.wireOp",EDGE,"E24.46.7.0"),sQuery(id+"F0.wireOp",EDGE,"E24.49.7.0"),sQuery(id+"F0.wireOp",EDGE,"E24.52.7.0"),sQuery(id+"F0.wireOp",EDGE,"E24.56.7.0"),sQuery(id+"F0.wireOp",EDGE,"E24.59.7.0"),sQuery(id+"F0.wireOp",EDGE,"E24.63.7.0"),sQuery(id+"F0.wireOp",EDGE,"E24.66.7.0"),sQuery(id+"F0.wireOp",EDGE,"E24.70.7.0"),sQuery(id+"F0.wireOp",EDGE,"E24.74.7.0")])]});
            var Q94;
            Q94=makeQuery(id+"F1.opExtrude","SWEPT_BODY",BODY,{"disambiguationData":[OSD([sQuery(id+"F0.wireOp",EDGE,"E1.bottom"),sQuery(id+"F0.wireOp",EDGE,"E1.top"),sQuery(id+"F0.wireOp",EDGE,"E1.left"),sQuery(id+"F0.wireOp",EDGE,"E1.right"),sQuery(id+"F0.wireOp",EDGE,"E2"),sQuery(id+"F0.wireOp",EDGE,"E3"),sQuery(id+"F0.wireOp",EDGE,"E4"),sQuery(id+"F0.wireOp",EDGE,"E5"),sQuery(id+"F0.wireOp",EDGE,"E6"),sQuery(id+"F0.wireOp",EDGE,"E7"),sQuery(id+"F0.wireOp",EDGE,"E8"),sQuery(id+"F0.wireOp",EDGE,"E9.MirrorCS"),sQuery(id+"F0.wireOp",EDGE,"E10.MirrorCS"),sQuery(id+"F0.wireOp",EDGE,"E11.MirrorCS"),sQuery(id+"F0.wireOp",EDGE,"E13.trimOffspring"),sQuery(id+"F0.wireOp",EDGE,"E14.trimOffspring"),sQuery(id+"F0.wireOp",EDGE,"E16.trimOffspring"),sQuery(id+"F0.wireOp",EDGE,"E17.trimOffspring"),sQuery(id+"F0.wireOp",EDGE,"E20"),sQuery(id+"F0.wireOp",EDGE,"E21")])]});
            var Q95;
            Q95=makeQuery(id+"F4.opExtrude","SWEPT_BODY",BODY,{"disambiguationData":[OSD([sQuery(id+"F0.wireOp",EDGE,"E23.3.0.1"),sQuery(id+"F0.wireOp",EDGE,"E23.3.0.2"),sQuery(id+"F0.wireOp",EDGE,"E23.3.0.3"),sQuery(id+"F0.wireOp",EDGE,"E23.3.0.4"),sQuery(id+"F0.wireOp",EDGE,"E23.3.0.11"),sQuery(id+"F0.wireOp",EDGE,"E23.3.0.12"),sQuery(id+"F0.wireOp",EDGE,"E23.3.0.13"),sQuery(id+"F0.wireOp",EDGE,"E23.3.0.14"),sQuery(id+"F0.wireOp",EDGE,"E23.3.0.15"),sQuery(id+"F0.wireOp",EDGE,"E23.3.0.16"),sQuery(id+"F0.wireOp",EDGE,"E23.3.0.18"),sQuery(id+"F0.wireOp",EDGE,"E23.3.0.19"),sQuery(id+"F0.wireOp",EDGE,"E23.3.0.20"),sQuery(id+"F0.wireOp",EDGE,"E23.3.0.21"),sQuery(id+"F0.wireOp",EDGE,"E23.3.0.22"),sQuery(id+"F0.wireOp",EDGE,"E23.3.0.23"),sQuery(id+"F0.wireOp",EDGE,"E23.3.0.24"),sQuery(id+"F0.wireOp",EDGE,"E23.3.0.25"),sQuery(id+"F0.wireOp",EDGE,"E23.3.0.26"),sQuery(id+"F0.wireOp",EDGE,"E23.3.0.27")])]});
            hole(context, id + "F13", {"style" : HoleStyle.C_BORE, "endStyle" : HoleEndStyle.THROUGH, "holeDiameter" : 3.5 * mm, "cBoreDiameter" : 6 * mm, "cBoreDepth" : 3.5 * mm, "majorDiameter" : 5 * mm, "isTappedThrough" : true, "tappedDepth" : 12 * mm, "tapClearance" : 3, "locations" : qUnion([Q0, Q1, Q2, Q3, Q4, Q5, Q6, Q7, Q8, Q9, Q10, Q11, Q12, Q13, Q14, Q15, Q16, Q17, Q18, Q19, Q20, Q21, Q22, Q23, Q24, Q25, Q26, Q27, Q28, Q29, Q30, Q31, Q32, Q33, Q34, Q35, Q36, Q37, Q38, Q39, Q40, Q41, Q42, Q43, Q44, Q45, Q46, Q47, Q48, Q49, Q50, Q51, Q52, Q53, Q54, Q55, Q56, Q57, Q58, Q59, Q60, Q61, Q62, Q63, Q64, Q65, Q66, Q67, Q68, Q69, Q70, Q71, Q72, Q73, Q74, Q75, Q76, Q77, Q78, Q79, Q80, Q81, Q82, Q83, Q84]), "scope" : qUnion([Q85, Q86, Q87, Q88, Q89, Q90, Q91, Q92, Q93, Q94, Q95])});
        }
        {
            var Q0;
            Q0=sQuery(id+"F12.wireOp",VERTEX,"E28.0.10.0");
            var Q1;
            Q1=sQuery(id+"F12.wireOp",VERTEX,"E30.0.24.0");
            var Q2;
            Q2=sQuery(id+"F12.wireOp",VERTEX,"E30.0.12.0");
            var Q3;
            Q3=sQuery(id+"F12.wireOp",VERTEX,"E30.0.16.0");
            var Q4;
            Q4=sQuery(id+"F12.wireOp",VERTEX,"E30.0.33.0");
            var Q5;
            Q5=sQuery(id+"F12.wireOp",VERTEX,"E30.0.32.0");
            var Q6;
            Q6=sQuery(id+"F12.wireOp",VERTEX,"E30.0.36.0");
            var Q7;
            Q7=sQuery(id+"F12.wireOp",VERTEX,"E30.0.28.0");
            var Q8;
            Q8=sQuery(id+"F12.wireOp",VERTEX,"E30.0.37.0");
            var Q9;
            Q9=sQuery(id+"F12.wireOp",VERTEX,"E30.0.4.0");
            var Q10;
            Q10=sQuery(id+"F12.wireOp",VERTEX,"E30.0.8.0");
            var Q11;
            Q11=sQuery(id+"F12.wireOp",VERTEX,"E30.0.20.0");
            var Q12;
            Q12=sQuery(id+"F12.wireOp",VERTEX,"E30.0.5.0");
            var Q13;
            Q13=sQuery(id+"F12.wireOp",VERTEX,"E29.1.0.0");
            var Q14;
            Q14=sQuery(id+"F12.wireOp",VERTEX,"E30.0.21.0");
            var Q15;
            Q15=sQuery(id+"F12.wireOp",VERTEX,"E30.0.17.0");
            var Q16;
            Q16=sQuery(id+"F12.wireOp",VERTEX,"E30.0.13.0");
            var Q17;
            Q17=sQuery(id+"F12.wireOp",VERTEX,"E30.0.9.0");
            var Q18;
            Q18=sQuery(id+"F12.wireOp",VERTEX,"E30.0.29.0");
            var Q19;
            Q19=sQuery(id+"F12.wireOp",VERTEX,"E30.0.25.0");
            var Q20;
            Q20=sQuery(id+"F12.wireOp",VERTEX,"E30.0.6.0");
            var Q21;
            Q21=sQuery(id+"F12.wireOp",VERTEX,"E29.2.0.0");
            var Q22;
            Q22=sQuery(id+"F12.wireOp",VERTEX,"E30.0.22.0");
            var Q23;
            Q23=sQuery(id+"F12.wireOp",VERTEX,"E30.0.18.0");
            var Q24;
            Q24=sQuery(id+"F12.wireOp",VERTEX,"E30.0.14.0");
            var Q25;
            Q25=sQuery(id+"F12.wireOp",VERTEX,"E30.0.10.0");
            var Q26;
            Q26=sQuery(id+"F12.wireOp",VERTEX,"E30.0.30.0");
            var Q27;
            Q27=sQuery(id+"F12.wireOp",VERTEX,"E30.0.26.0");
            var Q28;
            Q28=sQuery(id+"F12.wireOp",VERTEX,"E30.0.38.0");
            var Q29;
            Q29=sQuery(id+"F12.wireOp",VERTEX,"E30.0.34.0");
            var Q30;
            Q30=sQuery(id+"F12.wireOp",VERTEX,"E30.0.15.0");
            var Q31;
            Q31=sQuery(id+"F12.wireOp",VERTEX,"E30.0.11.0");
            var Q32;
            Q32=sQuery(id+"F12.wireOp",VERTEX,"E30.0.7.0");
            var Q33;
            Q33=sQuery(id+"F12.wireOp",VERTEX,"E30.0.3.0");
            var Q34;
            Q34=sQuery(id+"F12.wireOp",VERTEX,"E30.0.31.0");
            var Q35;
            Q35=sQuery(id+"F12.wireOp",VERTEX,"E30.0.27.0");
            var Q36;
            Q36=sQuery(id+"F12.wireOp",VERTEX,"E30.0.23.0");
            var Q37;
            Q37=sQuery(id+"F12.wireOp",VERTEX,"E30.0.19.0");
            var Q38;
            Q38=sQuery(id+"F12.wireOp",VERTEX,"E30.0.39.0");
            var Q39;
            Q39=sQuery(id+"F12.wireOp",VERTEX,"E30.0.35.0");
            var Q40;
            Q40=sQuery(id+"F12.wireOp",VERTEX,"E31.0.42.0");
            var Q41;
            Q41=sQuery(id+"F12.wireOp",VERTEX,"E31.0.43.0");
            var Q42;
            Q42=sQuery(id+"F12.wireOp",VERTEX,"E31.0.48.0");
            var Q43;
            Q43=sQuery(id+"F12.wireOp",VERTEX,"E31.0.44.0");
            var Q44;
            Q44=sQuery(id+"F12.wireOp",VERTEX,"E31.0.41.0");
            var Q45;
            Q45=sQuery(id+"F12.wireOp",VERTEX,"E31.0.49.0");
            var Q46;
            Q46=sQuery(id+"F12.wireOp",VERTEX,"E31.0.45.0");
            var Q47;
            Q47=sQuery(id+"F12.wireOp",VERTEX,"E31.0.46.0");
            var Q48;
            Q48=sQuery(id+"F12.wireOp",VERTEX,"E31.0.47.0");
            var Q49;
            Q49=sQuery(id+"F12.wireOp",VERTEX,"E31.0.40.0");
            var Q50;
            Q50=makeQuery(id+"F11.opExtrude","SWEPT_BODY",BODY,{"disambiguationData":[OSD([sQuery(id+"F0.wireOp",EDGE,"E24.3.10.0"),sQuery(id+"F0.wireOp",EDGE,"E24.6.10.0"),sQuery(id+"F0.wireOp",EDGE,"E24.9.10.0"),sQuery(id+"F0.wireOp",EDGE,"E24.12.10.0"),sQuery(id+"F0.wireOp",EDGE,"E24.21.10.0"),sQuery(id+"F0.wireOp",EDGE,"E24.24.10.0"),sQuery(id+"F0.wireOp",EDGE,"E24.27.10.0"),sQuery(id+"F0.wireOp",EDGE,"E24.30.10.0"),sQuery(id+"F0.wireOp",EDGE,"E24.33.10.0"),sQuery(id+"F0.wireOp",EDGE,"E24.36.10.0"),sQuery(id+"F0.wireOp",EDGE,"E24.43.10.0"),sQuery(id+"F0.wireOp",EDGE,"E24.46.10.0"),sQuery(id+"F0.wireOp",EDGE,"E24.49.10.0"),sQuery(id+"F0.wireOp",EDGE,"E24.52.10.0"),sQuery(id+"F0.wireOp",EDGE,"E24.56.10.0"),sQuery(id+"F0.wireOp",EDGE,"E24.59.10.0"),sQuery(id+"F0.wireOp",EDGE,"E24.63.10.0"),sQuery(id+"F0.wireOp",EDGE,"E24.66.10.0"),sQuery(id+"F0.wireOp",EDGE,"E24.70.10.0"),sQuery(id+"F0.wireOp",EDGE,"E24.74.10.0")])]});
            hole(context, id + "F14", {"style" : HoleStyle.C_BORE, "endStyle" : HoleEndStyle.THROUGH, "holeDiameter" : 3.5 * mm, "cBoreDiameter" : 6 * mm, "cBoreDepth" : 3.5 * mm, "majorDiameter" : 5 * mm, "isTappedThrough" : true, "tappedDepth" : 12 * mm, "tapClearance" : 3, "locations" : qUnion([Q0, Q1, Q2, Q3, Q4, Q5, Q6, Q7, Q8, Q9, Q10, Q11, Q12, Q13, Q14, Q15, Q16, Q17, Q18, Q19, Q20, Q21, Q22, Q23, Q24, Q25, Q26, Q27, Q28, Q29, Q30, Q31, Q32, Q33, Q34, Q35, Q36, Q37, Q38, Q39, Q40, Q41, Q42, Q43, Q44, Q45, Q46, Q47, Q48, Q49]), "scope" : qUnion([Q50])});
        }
        {
            var Q0;
            Q0=qCreatedBy(makeId("Front.planeOp"),FACE);
            var sketch = newSketch(context, id + "F15", { "sketchPlane" : qUnion([Q0])});
            skLineSegment(sketch, "E32", {"start": v(-50, -3.25) * mm, "end": v(-50, 6.75) * mm, "construction": true});
            skLineSegment(sketch, "E33", {"start": v(-50, 6.75) * mm, "end": v(-60, 6.75) * mm});
            skLineSegment(sketch, "E34", {"start": v(-60, 6.75) * mm, "end": v(-60, -1.25) * mm});
            skLineSegment(sketch, "E35", {"start": v(-60, -1.25) * mm, "end": v(-54.5, -1.25) * mm});
            skLineSegment(sketch, "E36", {"start": v(-54.5, -1.25) * mm, "end": v(-54.5, 0.25) * mm});
            skLineSegment(sketch, "E37", {"start": v(-54.5, 3.25) * mm, "end": v(-50, 3.25) * mm});
            skPoint(sketch, "E38", {"position": v(-57.5, 6.75) * mm});
            skArc(sketch, "E39", {"start": v(-54.5, 2.25) * mm, "mid": v(-55.5, 1.25) * mm, "end": v(-54.5, 0.25) * mm});
            skLineSegment(sketch, "E40.MirrorCS", {"start": v(-50, 6.75) * mm, "end": v(-40, 6.75) * mm});
            skPoint(sketch, "E41.MirrorP", {"position": v(-42.5, 6.75) * mm});
            skLineSegment(sketch, "E42.MirrorCS", {"start": v(-40, 6.75) * mm, "end": v(-40, -1.25) * mm});
            skLineSegment(sketch, "E43.MirrorCS", {"start": v(-40, -1.25) * mm, "end": v(-45.5, -1.25) * mm});
            skArc(sketch, "E44.MirrorCS", {"start": v(-45.5, 2.25) * mm, "mid": v(-44.5, 1.25) * mm, "end": v(-45.5, 0.25) * mm});
            skLineSegment(sketch, "E45", {"start": v(-54.5, 0.25) * mm, "end": v(-54.5, 2.25) * mm});
            skLineSegment(sketch, "E46", {"start": v(-54.5, 2.25) * mm, "end": v(-54.5, 3.25) * mm});
            skLineSegment(sketch, "E47.MirrorCS", {"start": v(-45.5, 3.25) * mm, "end": v(-50, 3.25) * mm});
            skLineSegment(sketch, "E48.MirrorCS", {"start": v(-45.5, 2.25) * mm, "end": v(-45.5, 3.25) * mm});
            skLineSegment(sketch, "E49.MirrorCS", {"start": v(-45.5, -1.25) * mm, "end": v(-45.5, 0.25) * mm});
            skPoint(sketch, "E50", {"position": v(-50, 4.95) * mm});
            skLineSegment(sketch, "E51", {"start": v(-60, 6.25) * mm, "end": v(-40, 6.25) * mm});
            skLineSegment(sketch, "E52.MirrorCS", {"start": v(-45.5, 0.25) * mm, "end": v(-45.5, 2.25) * mm});
            skLineSegment(sketch, "E53", {"start": v(-45.5, 3.25) * mm, "end": v(-4.15, 3.25) * mm, "construction": true});
            skLineSegment(sketch, "E54", {"start": v(-3.3, 1.25) * mm, "end": v(-54.5, 1.25) * mm, "construction": true});
            skLineSegment(sketch, "E55", {"start": v(-4.15, -3.25) * mm, "end": v(-50, -3.25) * mm, "construction": true});
            skLineSegment(sketch, "E56.1.0.0", {"start": v(-90, -3.25) * mm, "end": v(-90, 6.75) * mm, "construction": true});
            skLineSegment(sketch, "E56.1.0.1", {"start": v(-100, 6.75) * mm, "end": v(-100, -1.25) * mm});
            skLineSegment(sketch, "E56.1.0.2", {"start": v(-100, 6.25) * mm, "end": v(-80, 6.25) * mm});
            skPoint(sketch, "E56.1.0.3", {"position": v(-97.5, 6.75) * mm});
            skLineSegment(sketch, "E56.1.0.4", {"start": v(-90, 6.75) * mm, "end": v(-100, 6.75) * mm});
            skLineSegment(sketch, "E56.1.0.5", {"start": v(-90, 6.75) * mm, "end": v(-80, 6.75) * mm});
            skPoint(sketch, "E56.1.0.6", {"position": v(-82.5, 6.75) * mm});
            skLineSegment(sketch, "E56.1.0.7", {"start": v(-80, 6.75) * mm, "end": v(-80, -1.25) * mm});
            skLineSegment(sketch, "E56.1.0.8", {"start": v(-80, -1.25) * mm, "end": v(-85.5, -1.25) * mm});
            skLineSegment(sketch, "E56.1.0.9", {"start": v(-85.5, -1.25) * mm, "end": v(-85.5, 0.25) * mm});
            skLineSegment(sketch, "E56.1.0.10", {"start": v(-85.5, 0.25) * mm, "end": v(-85.5, 2.25) * mm});
            skArc(sketch, "E56.1.0.11", {"start": v(-85.5, 2.25) * mm, "mid": v(-84.5, 1.25) * mm, "end": v(-85.5, 0.25) * mm});
            skLineSegment(sketch, "E56.1.0.12", {"start": v(-85.5, 2.25) * mm, "end": v(-85.5, 3.25) * mm});
            skLineSegment(sketch, "E56.1.0.13", {"start": v(-85.5, 3.25) * mm, "end": v(-90, 3.25) * mm});
            skLineSegment(sketch, "E56.1.0.14", {"start": v(-94.5, 3.25) * mm, "end": v(-90, 3.25) * mm});
            skLineSegment(sketch, "E56.1.0.15", {"start": v(-94.5, 2.25) * mm, "end": v(-94.5, 3.25) * mm});
            skArc(sketch, "E56.1.0.16", {"start": v(-94.5, 2.25) * mm, "mid": v(-95.5, 1.25) * mm, "end": v(-94.5, 0.25) * mm});
            skLineSegment(sketch, "E56.1.0.17", {"start": v(-94.5, 0.25) * mm, "end": v(-94.5, 2.25) * mm});
            skLineSegment(sketch, "E56.1.0.18", {"start": v(-94.5, -1.25) * mm, "end": v(-94.5, 0.25) * mm});
            skLineSegment(sketch, "E56.1.0.19", {"start": v(-100, -1.25) * mm, "end": v(-94.5, -1.25) * mm});
            skLineSegment(sketch, "E56.direction1", {"start": v(-50, -3.25) * mm, "end": v(-90, -3.25) * mm, "construction": true});
            skPoint(sketch, "E57", {"position": v(-90, 4.95) * mm});
            skSolve(sketch);
        }
        {
            var Q0;
            {var subQ3=sQuery(id+"F15.wireOp",EDGE,"E35");Q0=makeQuery(id+"F15.imprint","IMPRINT",FACE,{"disambiguationData":[TD([[makeQuery(id+"F15.imprint","IMPRINT",EDGE,{"derivedFrom":subQ3}),1.0]])]});}
            var Q1;
            {var subQ4=sQuery(id+"F15.wireOp",EDGE,"E33");Q1=makeQuery(id+"F15.imprint","IMPRINT",FACE,{"disambiguationData":[TD([[makeQuery(id+"F15.imprint","IMPRINT",EDGE,{"derivedFrom":subQ4}),1.0]])]});}
            extrude(context, id + "F16", {"entities" : qUnion([Q0, Q1]), "depth" : (18.9 / 2) * mm, "offsetDistance" : 25 * mm});
        }
        {
            var Q0;
            Q0=makeQuery(id+"F16.opExtrude","CAP_FACE",FACE,{"disambiguationData":[OSD([sQuery(id+"F15.wireOp",EDGE,"E33"),sQuery(id+"F15.wireOp",EDGE,"E34"),sQuery(id+"F15.wireOp",EDGE,"E35"),sQuery(id+"F15.wireOp",EDGE,"E36"),sQuery(id+"F15.wireOp",EDGE,"E37"),sQuery(id+"F15.wireOp",EDGE,"E39"),sQuery(id+"F15.wireOp",EDGE,"E40.MirrorCS"),sQuery(id+"F15.wireOp",EDGE,"E42.MirrorCS"),sQuery(id+"F15.wireOp",EDGE,"E43.MirrorCS"),sQuery(id+"F15.wireOp",EDGE,"E44.MirrorCS"),sQuery(id+"F15.wireOp",EDGE,"E46"),sQuery(id+"F15.wireOp",EDGE,"E47.MirrorCS"),sQuery(id+"F15.wireOp",EDGE,"E48.MirrorCS"),sQuery(id+"F15.wireOp",EDGE,"E49.MirrorCS")])],"isStart":false});
            var sketch = newSketch(context, id + "F17", { "sketchPlane" : qUnion([Q0])});
            skLineSegment(sketch, "E58.0", {"start": v(-54.5, 0.25) * mm, "end": v(-54.5, 2.25) * mm});
            skLineSegment(sketch, "E59.0", {"start": v(-45.5, 0.25) * mm, "end": v(-45.5, 2.25) * mm});
            skLineSegment(sketch, "E60.0", {"start": v(-60, 6.25) * mm, "end": v(-40, 6.25) * mm});
            skSolve(sketch);
        }
        {
            var Q0;
            Q0=makeQuery(id+"F17.imprint","IMPRINT",FACE,{"disambiguationData":[TD([[makeQuery(id+"F17.imprint","IMPRINT",EDGE,{"derivedFrom":sQuery(id+"F17.wireOp",EDGE,"E58.0")}),1.0]])]});
            var Q1;
            {var subQ1=sQuery(id+"F17.wireOp",EDGE,"E60.0");Q1=makeQuery(id+"F17.imprint","IMPRINT",FACE,{"disambiguationData":[TD([[makeQuery(id+"F17.imprint","IMPRINT",EDGE,{"derivedFrom":subQ1}),-1.0]])]});}
            var Q2;
            Q2=makeQuery(id+"F17.imprint","IMPRINT",FACE,{"disambiguationData":[TD([[makeQuery(id+"F17.imprint","IMPRINT",EDGE,{"derivedFrom":sQuery(id+"F17.wireOp",EDGE,"E59.0")}),-1.0]])]});
            extrude(context, id + "F18", {"entities" : qUnion([Q0, Q1, Q2]), "operationType" : NewBodyOperationType.ADD, "depth" : ((28.9 - 18.9) / 2) * mm, "offsetDistance" : 25 * mm});
        }
        {
            var Q0;
            {var subQ2=sQuery(id+"F15.wireOp",EDGE,"E56.1.0.2");Q0=makeQuery(id+"F15.imprint","IMPRINT",FACE,{"disambiguationData":[TD([[makeQuery(id+"F15.imprint","IMPRINT",EDGE,{"derivedFrom":subQ2}),-1.0]])]});}
            var Q1;
            {var subQ2=sQuery(id+"F15.wireOp",EDGE,"E56.1.0.2");Q1=makeQuery(id+"F15.imprint","IMPRINT",FACE,{"disambiguationData":[TD([[makeQuery(id+"F15.imprint","IMPRINT",EDGE,{"derivedFrom":subQ2}),1.0]])]});}
            extrude(context, id + "F19", {"entities" : qUnion([Q0, Q1]), "depth" : (29.9 / 2) * mm, "offsetDistance" : 25 * mm});
        }
        {
            var Q0;
            Q0=makeQuery(id+"F19.opExtrude","CAP_FACE",FACE,{"disambiguationData":[OSD([sQuery(id+"F15.wireOp",EDGE,"E56.1.0.1"),sQuery(id+"F15.wireOp",EDGE,"E56.1.0.4"),sQuery(id+"F15.wireOp",EDGE,"E56.1.0.5"),sQuery(id+"F15.wireOp",EDGE,"E56.1.0.7"),sQuery(id+"F15.wireOp",EDGE,"E56.1.0.8"),sQuery(id+"F15.wireOp",EDGE,"E56.1.0.9"),sQuery(id+"F15.wireOp",EDGE,"E56.1.0.11"),sQuery(id+"F15.wireOp",EDGE,"E56.1.0.12"),sQuery(id+"F15.wireOp",EDGE,"E56.1.0.13"),sQuery(id+"F15.wireOp",EDGE,"E56.1.0.14"),sQuery(id+"F15.wireOp",EDGE,"E56.1.0.15"),sQuery(id+"F15.wireOp",EDGE,"E56.1.0.16"),sQuery(id+"F15.wireOp",EDGE,"E56.1.0.18"),sQuery(id+"F15.wireOp",EDGE,"E56.1.0.19")])],"isStart":false});
            var sketch = newSketch(context, id + "F20", { "sketchPlane" : qUnion([Q0])});
            skLineSegment(sketch, "E61.0", {"start": v(-94.5, 0.25) * mm, "end": v(-94.5, 2.25) * mm});
            skLineSegment(sketch, "E62.0", {"start": v(-85.5, 0.25) * mm, "end": v(-85.5, 2.25) * mm});
            skLineSegment(sketch, "E63.0", {"start": v(-100, 6.25) * mm, "end": v(-80, 6.25) * mm});
            skSolve(sketch);
        }
        {
            var Q0;
            {var subQ1=sQuery(id+"F20.wireOp",EDGE,"E63.0");Q0=makeQuery(id+"F20.imprint","IMPRINT",FACE,{"disambiguationData":[TD([[makeQuery(id+"F20.imprint","IMPRINT",EDGE,{"derivedFrom":subQ1}),-1.0]])]});}
            var Q1;
            Q1=makeQuery(id+"F20.imprint","IMPRINT",FACE,{"disambiguationData":[TD([[makeQuery(id+"F20.imprint","IMPRINT",EDGE,{"derivedFrom":sQuery(id+"F20.wireOp",EDGE,"E61.0")}),1.0]])]});
            var Q2;
            Q2=makeQuery(id+"F20.imprint","IMPRINT",FACE,{"disambiguationData":[TD([[makeQuery(id+"F20.imprint","IMPRINT",EDGE,{"derivedFrom":sQuery(id+"F20.wireOp",EDGE,"E62.0")}),-1.0]])]});
            extrude(context, id + "F21", {"entities" : qUnion([Q0, Q1, Q2]), "operationType" : NewBodyOperationType.ADD, "depth" : 5 * mm, "offsetDistance" : 25 * mm});
        }
        {
            var Q0;
            Q0=makeQuery(id+"F16.opExtrude","SWEPT_FACE",FACE,{"disambiguationData":[OSD([sQuery(id+"F15.wireOp",EDGE,"E33"),sQuery(id+"F15.wireOp",EDGE,"E40.MirrorCS")])]});
            var sketch = newSketch(context, id + "F22", { "sketchPlane" : qUnion([Q0])});
            skPoint(sketch, "E64", {"position": v(-57.5, -5) * mm});
            skPoint(sketch, "E65", {"position": v(-42.5, -5) * mm});
            skPoint(sketch, "E66", {"position": v(-82.5, -8) * mm});
            skPoint(sketch, "E67", {"position": v(-97.5, -8) * mm});
            skSolve(sketch);
        }
        {
            var Q0;
            Q0=sQuery(id+"F22.wireOp",VERTEX,"E64");
            var Q1;
            Q1=sQuery(id+"F22.wireOp",VERTEX,"E65");
            var Q2;
            Q2=sQuery(id+"F22.wireOp",VERTEX,"E66");
            var Q3;
            Q3=sQuery(id+"F22.wireOp",VERTEX,"E67");
            var Q4;
            Q4=makeQuery(id+"F16.opExtrude","SWEPT_BODY",BODY,{"disambiguationData":[OSD([sQuery(id+"F15.wireOp",EDGE,"E33"),sQuery(id+"F15.wireOp",EDGE,"E34"),sQuery(id+"F15.wireOp",EDGE,"E35"),sQuery(id+"F15.wireOp",EDGE,"E36"),sQuery(id+"F15.wireOp",EDGE,"E37"),sQuery(id+"F15.wireOp",EDGE,"E39"),sQuery(id+"F15.wireOp",EDGE,"E40.MirrorCS"),sQuery(id+"F15.wireOp",EDGE,"E42.MirrorCS"),sQuery(id+"F15.wireOp",EDGE,"E43.MirrorCS"),sQuery(id+"F15.wireOp",EDGE,"E44.MirrorCS"),sQuery(id+"F15.wireOp",EDGE,"E46"),sQuery(id+"F15.wireOp",EDGE,"E47.MirrorCS"),sQuery(id+"F15.wireOp",EDGE,"E48.MirrorCS"),sQuery(id+"F15.wireOp",EDGE,"E49.MirrorCS")])]});
            var Q5;
            Q5=makeQuery(id+"F19.opExtrude","SWEPT_BODY",BODY,{"disambiguationData":[OSD([sQuery(id+"F15.wireOp",EDGE,"E56.1.0.1"),sQuery(id+"F15.wireOp",EDGE,"E56.1.0.4"),sQuery(id+"F15.wireOp",EDGE,"E56.1.0.5"),sQuery(id+"F15.wireOp",EDGE,"E56.1.0.7"),sQuery(id+"F15.wireOp",EDGE,"E56.1.0.8"),sQuery(id+"F15.wireOp",EDGE,"E56.1.0.9"),sQuery(id+"F15.wireOp",EDGE,"E56.1.0.11"),sQuery(id+"F15.wireOp",EDGE,"E56.1.0.12"),sQuery(id+"F15.wireOp",EDGE,"E56.1.0.13"),sQuery(id+"F15.wireOp",EDGE,"E56.1.0.14"),sQuery(id+"F15.wireOp",EDGE,"E56.1.0.15"),sQuery(id+"F15.wireOp",EDGE,"E56.1.0.16"),sQuery(id+"F15.wireOp",EDGE,"E56.1.0.18"),sQuery(id+"F15.wireOp",EDGE,"E56.1.0.19")])]});
            hole(context, id + "F23", {"style" : HoleStyle.SIMPLE, "endStyle" : HoleEndStyle.BLIND, "standardTappedOrClearance" : lookupTablePath({ "standard" : "ISO", "engagement" : "75%", "pitch" : "0.5 mm", "size" : "M3", "type" : "Tapped" }), "standardBlindInLast" : lookupTablePath({ "standard" : "ISO", "engagement" : "75%", "pitch" : "0.5 mm", "size" : "M3", "type" : "Tapped" }), "holeDiameter" : 2.5 * mm, "majorDiameter" : 3 * mm, "showTappedDepth" : true, "holeDepth" : 4.1 * mm, "isTappedThrough" : true, "tappedDepth" : 2.6 * mm, "tapClearance" : 3, "locations" : qUnion([Q0, Q1, Q2, Q3]), "scope" : qUnion([Q4, Q5])});
        }
        {
            var Q0;
            Q0=makeQuery(id+"F19.opExtrude","SWEPT_BODY",BODY,{"disambiguationData":[OSD([sQuery(id+"F15.wireOp",EDGE,"E56.1.0.1"),sQuery(id+"F15.wireOp",EDGE,"E56.1.0.4"),sQuery(id+"F15.wireOp",EDGE,"E56.1.0.5"),sQuery(id+"F15.wireOp",EDGE,"E56.1.0.7"),sQuery(id+"F15.wireOp",EDGE,"E56.1.0.8"),sQuery(id+"F15.wireOp",EDGE,"E56.1.0.9"),sQuery(id+"F15.wireOp",EDGE,"E56.1.0.11"),sQuery(id+"F15.wireOp",EDGE,"E56.1.0.12"),sQuery(id+"F15.wireOp",EDGE,"E56.1.0.13"),sQuery(id+"F15.wireOp",EDGE,"E56.1.0.14"),sQuery(id+"F15.wireOp",EDGE,"E56.1.0.15"),sQuery(id+"F15.wireOp",EDGE,"E56.1.0.16"),sQuery(id+"F15.wireOp",EDGE,"E56.1.0.18"),sQuery(id+"F15.wireOp",EDGE,"E56.1.0.19")])]});
            var Q1;
            Q1=makeQuery(id+"F16.opExtrude","SWEPT_BODY",BODY,{"disambiguationData":[OSD([sQuery(id+"F15.wireOp",EDGE,"E33"),sQuery(id+"F15.wireOp",EDGE,"E34"),sQuery(id+"F15.wireOp",EDGE,"E35"),sQuery(id+"F15.wireOp",EDGE,"E36"),sQuery(id+"F15.wireOp",EDGE,"E37"),sQuery(id+"F15.wireOp",EDGE,"E39"),sQuery(id+"F15.wireOp",EDGE,"E40.MirrorCS"),sQuery(id+"F15.wireOp",EDGE,"E42.MirrorCS"),sQuery(id+"F15.wireOp",EDGE,"E43.MirrorCS"),sQuery(id+"F15.wireOp",EDGE,"E44.MirrorCS"),sQuery(id+"F15.wireOp",EDGE,"E46"),sQuery(id+"F15.wireOp",EDGE,"E47.MirrorCS"),sQuery(id+"F15.wireOp",EDGE,"E48.MirrorCS"),sQuery(id+"F15.wireOp",EDGE,"E49.MirrorCS")])]});
            var Q2;
            {var subQ2=sQuery(id+"F15.wireOp",EDGE,"E56.1.0.2");Q2=makeQuery(id+"F15.imprint","IMPRINT",FACE,{"disambiguationData":[TD([[makeQuery(id+"F15.imprint","IMPRINT",EDGE,{"derivedFrom":subQ2}),-1.0]])]});}
            mirror(context, id + "F24", {"operationType" : NewBodyOperationType.ADD, "entities" : qUnion([Q0, Q1]), "mirrorPlane" : qUnion([Q2])});
        }
        {
            var Q0;
            Q0=makeQuery(id+"F16.opExtrude","CAP_EDGE",EDGE,{"disambiguationData":[OSD([sQuery(id+"F15.wireOp",EDGE,"E33"),sQuery(id+"F15.wireOp",EDGE,"E40.MirrorCS")])],"isStart":false});
            var Q1;
            Q1=makeQuery(id+"F24.opPattern","COPY",EDGE,{"derivedFrom":makeQuery(id+"F16.opExtrude","CAP_EDGE",EDGE,{"disambiguationData":[OSD([sQuery(id+"F15.wireOp",EDGE,"E33"),sQuery(id+"F15.wireOp",EDGE,"E40.MirrorCS")])],"isStart":false}),"instanceName":"1"});
            var Q2;
            {var subQ0=makeQuery(id+"F16.opExtrude","SWEPT_EDGE",EDGE,{"disambiguationData":[OSD([sQuery(id+"F15.wireOp",EDGE,"E40.MirrorCS"),sQuery(id+"F15.wireOp",EDGE,"E42.MirrorCS")])]});Q2=makeQuery(id+"F24.boolean.opBoolean","MERGE",EDGE,{"derivedFrom":[subQ0,makeQuery(id+"F24.opPattern","COPY",EDGE,{"derivedFrom":subQ0,"instanceName":"1"})]});}
            var Q3;
            {var subQ0=makeQuery(id+"F16.opExtrude","SWEPT_EDGE",EDGE,{"disambiguationData":[OSD([sQuery(id+"F15.wireOp",EDGE,"E33"),sQuery(id+"F15.wireOp",EDGE,"E34")])]});Q3=makeQuery(id+"F24.boolean.opBoolean","MERGE",EDGE,{"derivedFrom":[subQ0,makeQuery(id+"F24.opPattern","COPY",EDGE,{"derivedFrom":subQ0,"instanceName":"1"})]});}
            var Q4;
            {var subQ0=makeQuery(id+"F19.opExtrude","SWEPT_EDGE",EDGE,{"disambiguationData":[OSD([sQuery(id+"F15.wireOp",EDGE,"E56.1.0.5"),sQuery(id+"F15.wireOp",EDGE,"E56.1.0.7")])]});Q4=makeQuery(id+"F24.boolean.opBoolean","MERGE",EDGE,{"derivedFrom":[subQ0,makeQuery(id+"F24.opPattern","COPY",EDGE,{"derivedFrom":subQ0,"instanceName":"1"})]});}
            var Q5;
            Q5=makeQuery(id+"F19.opExtrude","CAP_EDGE",EDGE,{"disambiguationData":[OSD([sQuery(id+"F15.wireOp",EDGE,"E56.1.0.4"),sQuery(id+"F15.wireOp",EDGE,"E56.1.0.5")])],"isStart":false});
            var Q6;
            Q6=makeQuery(id+"F24.opPattern","COPY",EDGE,{"derivedFrom":makeQuery(id+"F19.opExtrude","CAP_EDGE",EDGE,{"disambiguationData":[OSD([sQuery(id+"F15.wireOp",EDGE,"E56.1.0.4"),sQuery(id+"F15.wireOp",EDGE,"E56.1.0.5")])],"isStart":false}),"instanceName":"1"});
            var Q7;
            {var subQ0=makeQuery(id+"F19.opExtrude","SWEPT_EDGE",EDGE,{"disambiguationData":[OSD([sQuery(id+"F15.wireOp",EDGE,"E56.1.0.1"),sQuery(id+"F15.wireOp",EDGE,"E56.1.0.4")])]});Q7=makeQuery(id+"F24.boolean.opBoolean","MERGE",EDGE,{"derivedFrom":[subQ0,makeQuery(id+"F24.opPattern","COPY",EDGE,{"derivedFrom":subQ0,"instanceName":"1"})]});}
            chamfer(context, id + "F25", {"entities" : qUnion([Q0, Q1, Q2, Q3, Q4, Q5, Q6, Q7]), "width" : 0.5 * mm, "tangentPropagation" : true});
        }
    });
